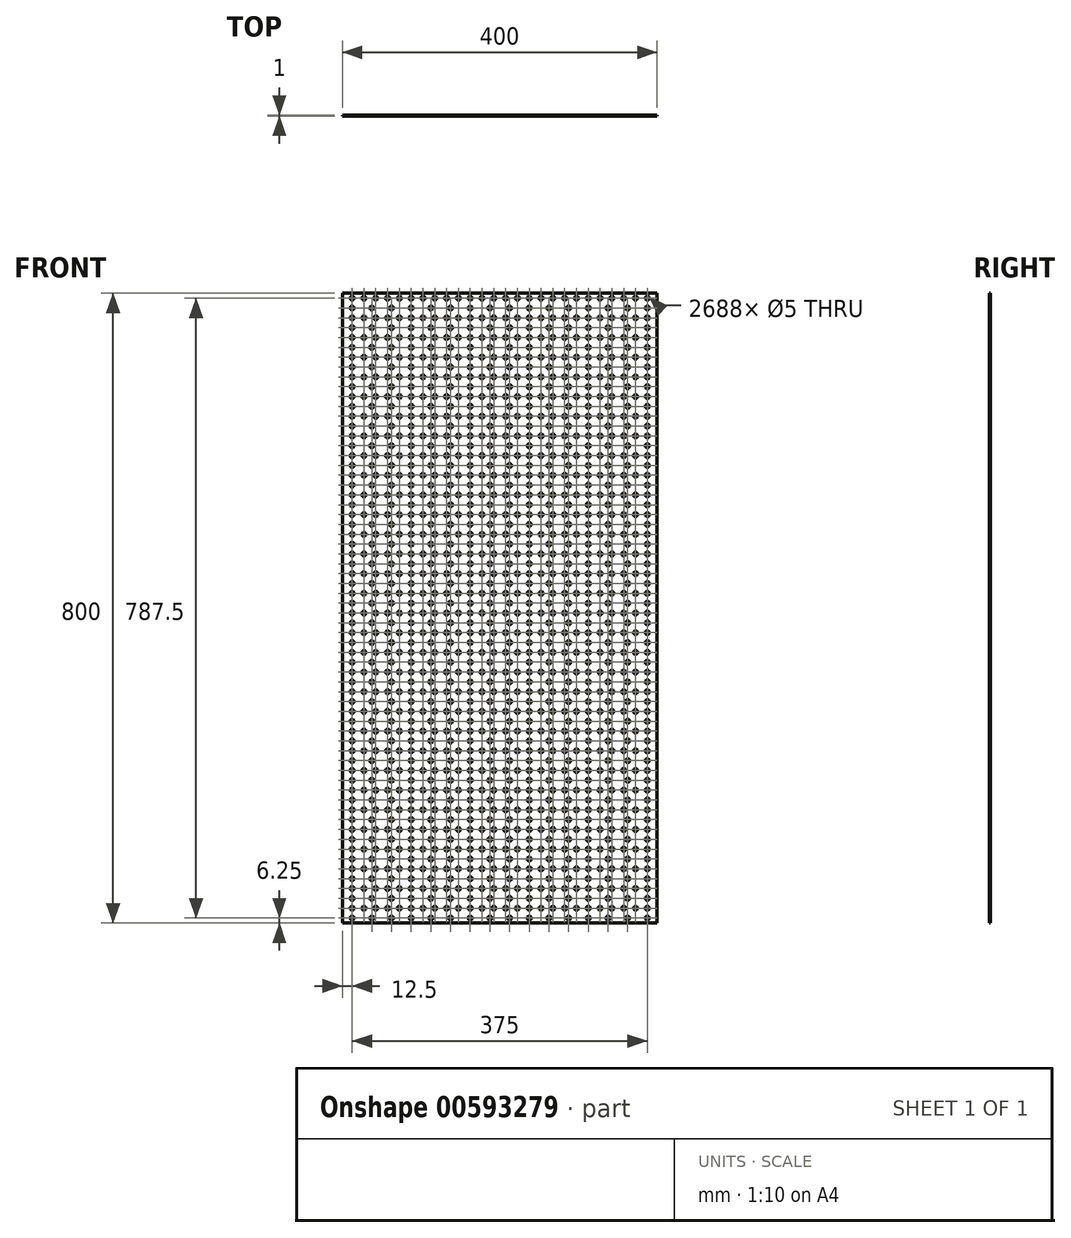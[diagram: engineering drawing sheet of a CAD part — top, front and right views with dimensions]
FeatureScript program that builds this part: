
annotation { "Feature Type Name" : "Feature", "Feature Type Description" : "" }
export const myFeature = defineFeature(function(context is Context, id is Id, definition is map)
    precondition{}
    {
        {
            var Q0;
            Q0=qCreatedBy(makeId("Front.planeOp"),FACE);
            var sketch = newSketch(context, id + "F0", { "sketchPlane" : qUnion([Q0])});
            skLineSegment(sketch, "E0.bottom", {"start": v(200, 400) * mm, "end": v(-200, 400) * mm});
            skLineSegment(sketch, "E0.top", {"start": v(200, -400) * mm, "end": v(-200, -400) * mm});
            skLineSegment(sketch, "E0.left", {"start": v(200, 400) * mm, "end": v(200, -400) * mm});
            skLineSegment(sketch, "E0.right", {"start": v(-200, 400) * mm, "end": v(-200, -400) * mm});
            skPoint(sketch, "E0.middle", {"position": v(0, 0) * mm});
            skCircle(sketch, "E1", {"center": v(-187.5, -393.75) * mm, "radius": 2.5 * mm});
            skCircle(sketch, "E2.1.0.0", {"center": v(-162.5, -393.75) * mm, "radius": 2.5 * mm});
            skCircle(sketch, "E2.2.0.0", {"center": v(-137.5, -393.75) * mm, "radius": 2.5 * mm});
            skCircle(sketch, "E2.3.0.0", {"center": v(-112.5, -393.75) * mm, "radius": 2.5 * mm});
            skCircle(sketch, "E2.4.0.0", {"center": v(-87.5, -393.75) * mm, "radius": 2.5 * mm});
            skCircle(sketch, "E2.5.0.0", {"center": v(-62.5, -393.75) * mm, "radius": 2.5 * mm});
            skCircle(sketch, "E2.6.0.0", {"center": v(-37.5, -393.75) * mm, "radius": 2.5 * mm});
            skCircle(sketch, "E2.7.0.0", {"center": v(-12.5, -393.75) * mm, "radius": 2.5 * mm});
            skCircle(sketch, "E2.8.0.0", {"center": v(12.5, -393.75) * mm, "radius": 2.5 * mm});
            skCircle(sketch, "E2.9.0.0", {"center": v(37.5, -393.75) * mm, "radius": 2.5 * mm});
            skCircle(sketch, "E2.10.0.0", {"center": v(62.5, -393.75) * mm, "radius": 2.5 * mm});
            skCircle(sketch, "E2.11.0.0", {"center": v(87.5, -393.75) * mm, "radius": 2.5 * mm});
            skCircle(sketch, "E2.12.0.0", {"center": v(112.5, -393.75) * mm, "radius": 2.5 * mm});
            skCircle(sketch, "E2.13.0.0", {"center": v(137.5, -393.75) * mm, "radius": 2.5 * mm});
            skCircle(sketch, "E2.14.0.0", {"center": v(162.5, -393.75) * mm, "radius": 2.5 * mm});
            skCircle(sketch, "E2.15.0.0", {"center": v(187.5, -393.75) * mm, "radius": 2.5 * mm});
            skLineSegment(sketch, "E2.direction1", {"start": v(-187.5, -393.75) * mm, "end": v(-162.5, -393.75) * mm, "construction": true});
            skCircle(sketch, "E3.0.1.0", {"center": v(187.5, -368.75) * mm, "radius": 2.5 * mm});
            skCircle(sketch, "E3.0.1.1", {"center": v(37.5, -368.75) * mm, "radius": 2.5 * mm});
            skCircle(sketch, "E3.0.1.2", {"center": v(137.5, -368.75) * mm, "radius": 2.5 * mm});
            skCircle(sketch, "E3.0.1.3", {"center": v(62.5, -368.75) * mm, "radius": 2.5 * mm});
            skCircle(sketch, "E3.0.1.4", {"center": v(87.5, -368.75) * mm, "radius": 2.5 * mm});
            skCircle(sketch, "E3.0.1.5", {"center": v(-137.5, -368.75) * mm, "radius": 2.5 * mm});
            skCircle(sketch, "E3.0.1.6", {"center": v(-112.5, -368.75) * mm, "radius": 2.5 * mm});
            skCircle(sketch, "E3.0.1.7", {"center": v(-87.5, -368.75) * mm, "radius": 2.5 * mm});
            skCircle(sketch, "E3.0.1.8", {"center": v(-62.5, -368.75) * mm, "radius": 2.5 * mm});
            skCircle(sketch, "E3.0.1.9", {"center": v(-37.5, -368.75) * mm, "radius": 2.5 * mm});
            skCircle(sketch, "E3.0.1.10", {"center": v(-12.5, -368.75) * mm, "radius": 2.5 * mm});
            skCircle(sketch, "E3.0.1.11", {"center": v(12.5, -368.75) * mm, "radius": 2.5 * mm});
            skCircle(sketch, "E3.0.1.12", {"center": v(162.5, -368.75) * mm, "radius": 2.5 * mm});
            skCircle(sketch, "E3.0.1.13", {"center": v(112.5, -368.75) * mm, "radius": 2.5 * mm});
            skCircle(sketch, "E3.0.1.14", {"center": v(-187.5, -368.75) * mm, "radius": 2.5 * mm});
            skCircle(sketch, "E3.0.1.15", {"center": v(-162.5, -368.75) * mm, "radius": 2.5 * mm});
            skCircle(sketch, "E3.0.2.0", {"center": v(187.5, -343.75) * mm, "radius": 2.5 * mm});
            skCircle(sketch, "E3.0.2.1", {"center": v(37.5, -343.75) * mm, "radius": 2.5 * mm});
            skCircle(sketch, "E3.0.2.2", {"center": v(137.5, -343.75) * mm, "radius": 2.5 * mm});
            skCircle(sketch, "E3.0.2.3", {"center": v(62.5, -343.75) * mm, "radius": 2.5 * mm});
            skCircle(sketch, "E3.0.2.4", {"center": v(87.5, -343.75) * mm, "radius": 2.5 * mm});
            skCircle(sketch, "E3.0.2.5", {"center": v(-137.5, -343.75) * mm, "radius": 2.5 * mm});
            skCircle(sketch, "E3.0.2.6", {"center": v(-112.5, -343.75) * mm, "radius": 2.5 * mm});
            skCircle(sketch, "E3.0.2.7", {"center": v(-87.5, -343.75) * mm, "radius": 2.5 * mm});
            skCircle(sketch, "E3.0.2.8", {"center": v(-62.5, -343.75) * mm, "radius": 2.5 * mm});
            skCircle(sketch, "E3.0.2.9", {"center": v(-37.5, -343.75) * mm, "radius": 2.5 * mm});
            skCircle(sketch, "E3.0.2.10", {"center": v(-12.5, -343.75) * mm, "radius": 2.5 * mm});
            skCircle(sketch, "E3.0.2.11", {"center": v(12.5, -343.75) * mm, "radius": 2.5 * mm});
            skCircle(sketch, "E3.0.2.12", {"center": v(162.5, -343.75) * mm, "radius": 2.5 * mm});
            skCircle(sketch, "E3.0.2.13", {"center": v(112.5, -343.75) * mm, "radius": 2.5 * mm});
            skCircle(sketch, "E3.0.2.14", {"center": v(-187.5, -343.75) * mm, "radius": 2.5 * mm});
            skCircle(sketch, "E3.0.2.15", {"center": v(-162.5, -343.75) * mm, "radius": 2.5 * mm});
            skCircle(sketch, "E3.0.3.0", {"center": v(187.5, -318.75) * mm, "radius": 2.5 * mm});
            skCircle(sketch, "E3.0.3.1", {"center": v(37.5, -318.75) * mm, "radius": 2.5 * mm});
            skCircle(sketch, "E3.0.3.2", {"center": v(137.5, -318.75) * mm, "radius": 2.5 * mm});
            skCircle(sketch, "E3.0.3.3", {"center": v(62.5, -318.75) * mm, "radius": 2.5 * mm});
            skCircle(sketch, "E3.0.3.4", {"center": v(87.5, -318.75) * mm, "radius": 2.5 * mm});
            skCircle(sketch, "E3.0.3.5", {"center": v(-137.5, -318.75) * mm, "radius": 2.5 * mm});
            skCircle(sketch, "E3.0.3.6", {"center": v(-112.5, -318.75) * mm, "radius": 2.5 * mm});
            skCircle(sketch, "E3.0.3.7", {"center": v(-87.5, -318.75) * mm, "radius": 2.5 * mm});
            skCircle(sketch, "E3.0.3.8", {"center": v(-62.5, -318.75) * mm, "radius": 2.5 * mm});
            skCircle(sketch, "E3.0.3.9", {"center": v(-37.5, -318.75) * mm, "radius": 2.5 * mm});
            skCircle(sketch, "E3.0.3.10", {"center": v(-12.5, -318.75) * mm, "radius": 2.5 * mm});
            skCircle(sketch, "E3.0.3.11", {"center": v(12.5, -318.75) * mm, "radius": 2.5 * mm});
            skCircle(sketch, "E3.0.3.12", {"center": v(162.5, -318.75) * mm, "radius": 2.5 * mm});
            skCircle(sketch, "E3.0.3.13", {"center": v(112.5, -318.75) * mm, "radius": 2.5 * mm});
            skCircle(sketch, "E3.0.3.14", {"center": v(-187.5, -318.75) * mm, "radius": 2.5 * mm});
            skCircle(sketch, "E3.0.3.15", {"center": v(-162.5, -318.75) * mm, "radius": 2.5 * mm});
            skCircle(sketch, "E3.0.4.0", {"center": v(187.5, -293.75) * mm, "radius": 2.5 * mm});
            skCircle(sketch, "E3.0.4.1", {"center": v(37.5, -293.75) * mm, "radius": 2.5 * mm});
            skCircle(sketch, "E3.0.4.2", {"center": v(137.5, -293.75) * mm, "radius": 2.5 * mm});
            skCircle(sketch, "E3.0.4.3", {"center": v(62.5, -293.75) * mm, "radius": 2.5 * mm});
            skCircle(sketch, "E3.0.4.4", {"center": v(87.5, -293.75) * mm, "radius": 2.5 * mm});
            skCircle(sketch, "E3.0.4.5", {"center": v(-137.5, -293.75) * mm, "radius": 2.5 * mm});
            skCircle(sketch, "E3.0.4.6", {"center": v(-112.5, -293.75) * mm, "radius": 2.5 * mm});
            skCircle(sketch, "E3.0.4.7", {"center": v(-87.5, -293.75) * mm, "radius": 2.5 * mm});
            skCircle(sketch, "E3.0.4.8", {"center": v(-62.5, -293.75) * mm, "radius": 2.5 * mm});
            skCircle(sketch, "E3.0.4.9", {"center": v(-37.5, -293.75) * mm, "radius": 2.5 * mm});
            skCircle(sketch, "E3.0.4.10", {"center": v(-12.5, -293.75) * mm, "radius": 2.5 * mm});
            skCircle(sketch, "E3.0.4.11", {"center": v(12.5, -293.75) * mm, "radius": 2.5 * mm});
            skCircle(sketch, "E3.0.4.12", {"center": v(162.5, -293.75) * mm, "radius": 2.5 * mm});
            skCircle(sketch, "E3.0.4.13", {"center": v(112.5, -293.75) * mm, "radius": 2.5 * mm});
            skCircle(sketch, "E3.0.4.14", {"center": v(-187.5, -293.75) * mm, "radius": 2.5 * mm});
            skCircle(sketch, "E3.0.4.15", {"center": v(-162.5, -293.75) * mm, "radius": 2.5 * mm});
            skCircle(sketch, "E3.0.5.0", {"center": v(187.5, -268.75) * mm, "radius": 2.5 * mm});
            skCircle(sketch, "E3.0.5.1", {"center": v(37.5, -268.75) * mm, "radius": 2.5 * mm});
            skCircle(sketch, "E3.0.5.2", {"center": v(137.5, -268.75) * mm, "radius": 2.5 * mm});
            skCircle(sketch, "E3.0.5.3", {"center": v(62.5, -268.75) * mm, "radius": 2.5 * mm});
            skCircle(sketch, "E3.0.5.4", {"center": v(87.5, -268.75) * mm, "radius": 2.5 * mm});
            skCircle(sketch, "E3.0.5.5", {"center": v(-137.5, -268.75) * mm, "radius": 2.5 * mm});
            skCircle(sketch, "E3.0.5.6", {"center": v(-112.5, -268.75) * mm, "radius": 2.5 * mm});
            skCircle(sketch, "E3.0.5.7", {"center": v(-87.5, -268.75) * mm, "radius": 2.5 * mm});
            skCircle(sketch, "E3.0.5.8", {"center": v(-62.5, -268.75) * mm, "radius": 2.5 * mm});
            skCircle(sketch, "E3.0.5.9", {"center": v(-37.5, -268.75) * mm, "radius": 2.5 * mm});
            skCircle(sketch, "E3.0.5.10", {"center": v(-12.5, -268.75) * mm, "radius": 2.5 * mm});
            skCircle(sketch, "E3.0.5.11", {"center": v(12.5, -268.75) * mm, "radius": 2.5 * mm});
            skCircle(sketch, "E3.0.5.12", {"center": v(162.5, -268.75) * mm, "radius": 2.5 * mm});
            skCircle(sketch, "E3.0.5.13", {"center": v(112.5, -268.75) * mm, "radius": 2.5 * mm});
            skCircle(sketch, "E3.0.5.14", {"center": v(-187.5, -268.75) * mm, "radius": 2.5 * mm});
            skCircle(sketch, "E3.0.5.15", {"center": v(-162.5, -268.75) * mm, "radius": 2.5 * mm});
            skCircle(sketch, "E3.0.6.0", {"center": v(187.5, -243.75) * mm, "radius": 2.5 * mm});
            skCircle(sketch, "E3.0.6.1", {"center": v(37.5, -243.75) * mm, "radius": 2.5 * mm});
            skCircle(sketch, "E3.0.6.2", {"center": v(137.5, -243.75) * mm, "radius": 2.5 * mm});
            skCircle(sketch, "E3.0.6.3", {"center": v(62.5, -243.75) * mm, "radius": 2.5 * mm});
            skCircle(sketch, "E3.0.6.4", {"center": v(87.5, -243.75) * mm, "radius": 2.5 * mm});
            skCircle(sketch, "E3.0.6.5", {"center": v(-137.5, -243.75) * mm, "radius": 2.5 * mm});
            skCircle(sketch, "E3.0.6.6", {"center": v(-112.5, -243.75) * mm, "radius": 2.5 * mm});
            skCircle(sketch, "E3.0.6.7", {"center": v(-87.5, -243.75) * mm, "radius": 2.5 * mm});
            skCircle(sketch, "E3.0.6.8", {"center": v(-62.5, -243.75) * mm, "radius": 2.5 * mm});
            skCircle(sketch, "E3.0.6.9", {"center": v(-37.5, -243.75) * mm, "radius": 2.5 * mm});
            skCircle(sketch, "E3.0.6.10", {"center": v(-12.5, -243.75) * mm, "radius": 2.5 * mm});
            skCircle(sketch, "E3.0.6.11", {"center": v(12.5, -243.75) * mm, "radius": 2.5 * mm});
            skCircle(sketch, "E3.0.6.12", {"center": v(162.5, -243.75) * mm, "radius": 2.5 * mm});
            skCircle(sketch, "E3.0.6.13", {"center": v(112.5, -243.75) * mm, "radius": 2.5 * mm});
            skCircle(sketch, "E3.0.6.14", {"center": v(-187.5, -243.75) * mm, "radius": 2.5 * mm});
            skCircle(sketch, "E3.0.6.15", {"center": v(-162.5, -243.75) * mm, "radius": 2.5 * mm});
            skCircle(sketch, "E3.0.7.0", {"center": v(187.5, -218.75) * mm, "radius": 2.5 * mm});
            skCircle(sketch, "E3.0.7.1", {"center": v(37.5, -218.75) * mm, "radius": 2.5 * mm});
            skCircle(sketch, "E3.0.7.2", {"center": v(137.5, -218.75) * mm, "radius": 2.5 * mm});
            skCircle(sketch, "E3.0.7.3", {"center": v(62.5, -218.75) * mm, "radius": 2.5 * mm});
            skCircle(sketch, "E3.0.7.4", {"center": v(87.5, -218.75) * mm, "radius": 2.5 * mm});
            skCircle(sketch, "E3.0.7.5", {"center": v(-137.5, -218.75) * mm, "radius": 2.5 * mm});
            skCircle(sketch, "E3.0.7.6", {"center": v(-112.5, -218.75) * mm, "radius": 2.5 * mm});
            skCircle(sketch, "E3.0.7.7", {"center": v(-87.5, -218.75) * mm, "radius": 2.5 * mm});
            skCircle(sketch, "E3.0.7.8", {"center": v(-62.5, -218.75) * mm, "radius": 2.5 * mm});
            skCircle(sketch, "E3.0.7.9", {"center": v(-37.5, -218.75) * mm, "radius": 2.5 * mm});
            skCircle(sketch, "E3.0.7.10", {"center": v(-12.5, -218.75) * mm, "radius": 2.5 * mm});
            skCircle(sketch, "E3.0.7.11", {"center": v(12.5, -218.75) * mm, "radius": 2.5 * mm});
            skCircle(sketch, "E3.0.7.12", {"center": v(162.5, -218.75) * mm, "radius": 2.5 * mm});
            skCircle(sketch, "E3.0.7.13", {"center": v(112.5, -218.75) * mm, "radius": 2.5 * mm});
            skCircle(sketch, "E3.0.7.14", {"center": v(-187.5, -218.75) * mm, "radius": 2.5 * mm});
            skCircle(sketch, "E3.0.7.15", {"center": v(-162.5, -218.75) * mm, "radius": 2.5 * mm});
            skCircle(sketch, "E3.0.8.0", {"center": v(187.5, -193.75) * mm, "radius": 2.5 * mm});
            skCircle(sketch, "E3.0.8.1", {"center": v(37.5, -193.75) * mm, "radius": 2.5 * mm});
            skCircle(sketch, "E3.0.8.2", {"center": v(137.5, -193.75) * mm, "radius": 2.5 * mm});
            skCircle(sketch, "E3.0.8.3", {"center": v(62.5, -193.75) * mm, "radius": 2.5 * mm});
            skCircle(sketch, "E3.0.8.4", {"center": v(87.5, -193.75) * mm, "radius": 2.5 * mm});
            skCircle(sketch, "E3.0.8.5", {"center": v(-137.5, -193.75) * mm, "radius": 2.5 * mm});
            skCircle(sketch, "E3.0.8.6", {"center": v(-112.5, -193.75) * mm, "radius": 2.5 * mm});
            skCircle(sketch, "E3.0.8.7", {"center": v(-87.5, -193.75) * mm, "radius": 2.5 * mm});
            skCircle(sketch, "E3.0.8.8", {"center": v(-62.5, -193.75) * mm, "radius": 2.5 * mm});
            skCircle(sketch, "E3.0.8.9", {"center": v(-37.5, -193.75) * mm, "radius": 2.5 * mm});
            skCircle(sketch, "E3.0.8.10", {"center": v(-12.5, -193.75) * mm, "radius": 2.5 * mm});
            skCircle(sketch, "E3.0.8.11", {"center": v(12.5, -193.75) * mm, "radius": 2.5 * mm});
            skCircle(sketch, "E3.0.8.12", {"center": v(162.5, -193.75) * mm, "radius": 2.5 * mm});
            skCircle(sketch, "E3.0.8.13", {"center": v(112.5, -193.75) * mm, "radius": 2.5 * mm});
            skCircle(sketch, "E3.0.8.14", {"center": v(-187.5, -193.75) * mm, "radius": 2.5 * mm});
            skCircle(sketch, "E3.0.8.15", {"center": v(-162.5, -193.75) * mm, "radius": 2.5 * mm});
            skCircle(sketch, "E3.0.9.0", {"center": v(187.5, -168.75) * mm, "radius": 2.5 * mm});
            skCircle(sketch, "E3.0.9.1", {"center": v(37.5, -168.75) * mm, "radius": 2.5 * mm});
            skCircle(sketch, "E3.0.9.2", {"center": v(137.5, -168.75) * mm, "radius": 2.5 * mm});
            skCircle(sketch, "E3.0.9.3", {"center": v(62.5, -168.75) * mm, "radius": 2.5 * mm});
            skCircle(sketch, "E3.0.9.4", {"center": v(87.5, -168.75) * mm, "radius": 2.5 * mm});
            skCircle(sketch, "E3.0.9.5", {"center": v(-137.5, -168.75) * mm, "radius": 2.5 * mm});
            skCircle(sketch, "E3.0.9.6", {"center": v(-112.5, -168.75) * mm, "radius": 2.5 * mm});
            skCircle(sketch, "E3.0.9.7", {"center": v(-87.5, -168.75) * mm, "radius": 2.5 * mm});
            skCircle(sketch, "E3.0.9.8", {"center": v(-62.5, -168.75) * mm, "radius": 2.5 * mm});
            skCircle(sketch, "E3.0.9.9", {"center": v(-37.5, -168.75) * mm, "radius": 2.5 * mm});
            skCircle(sketch, "E3.0.9.10", {"center": v(-12.5, -168.75) * mm, "radius": 2.5 * mm});
            skCircle(sketch, "E3.0.9.11", {"center": v(12.5, -168.75) * mm, "radius": 2.5 * mm});
            skCircle(sketch, "E3.0.9.12", {"center": v(162.5, -168.75) * mm, "radius": 2.5 * mm});
            skCircle(sketch, "E3.0.9.13", {"center": v(112.5, -168.75) * mm, "radius": 2.5 * mm});
            skCircle(sketch, "E3.0.9.14", {"center": v(-187.5, -168.75) * mm, "radius": 2.5 * mm});
            skCircle(sketch, "E3.0.9.15", {"center": v(-162.5, -168.75) * mm, "radius": 2.5 * mm});
            skCircle(sketch, "E3.0.10.0", {"center": v(187.5, -143.75) * mm, "radius": 2.5 * mm});
            skCircle(sketch, "E3.0.10.1", {"center": v(37.5, -143.75) * mm, "radius": 2.5 * mm});
            skCircle(sketch, "E3.0.10.2", {"center": v(137.5, -143.75) * mm, "radius": 2.5 * mm});
            skCircle(sketch, "E3.0.10.3", {"center": v(62.5, -143.75) * mm, "radius": 2.5 * mm});
            skCircle(sketch, "E3.0.10.4", {"center": v(87.5, -143.75) * mm, "radius": 2.5 * mm});
            skCircle(sketch, "E3.0.10.5", {"center": v(-137.5, -143.75) * mm, "radius": 2.5 * mm});
            skCircle(sketch, "E3.0.10.6", {"center": v(-112.5, -143.75) * mm, "radius": 2.5 * mm});
            skCircle(sketch, "E3.0.10.7", {"center": v(-87.5, -143.75) * mm, "radius": 2.5 * mm});
            skCircle(sketch, "E3.0.10.8", {"center": v(-62.5, -143.75) * mm, "radius": 2.5 * mm});
            skCircle(sketch, "E3.0.10.9", {"center": v(-37.5, -143.75) * mm, "radius": 2.5 * mm});
            skCircle(sketch, "E3.0.10.10", {"center": v(-12.5, -143.75) * mm, "radius": 2.5 * mm});
            skCircle(sketch, "E3.0.10.11", {"center": v(12.5, -143.75) * mm, "radius": 2.5 * mm});
            skCircle(sketch, "E3.0.10.12", {"center": v(162.5, -143.75) * mm, "radius": 2.5 * mm});
            skCircle(sketch, "E3.0.10.13", {"center": v(112.5, -143.75) * mm, "radius": 2.5 * mm});
            skCircle(sketch, "E3.0.10.14", {"center": v(-187.5, -143.75) * mm, "radius": 2.5 * mm});
            skCircle(sketch, "E3.0.10.15", {"center": v(-162.5, -143.75) * mm, "radius": 2.5 * mm});
            skCircle(sketch, "E3.0.11.0", {"center": v(187.5, -118.75) * mm, "radius": 2.5 * mm});
            skCircle(sketch, "E3.0.11.1", {"center": v(37.5, -118.75) * mm, "radius": 2.5 * mm});
            skCircle(sketch, "E3.0.11.2", {"center": v(137.5, -118.75) * mm, "radius": 2.5 * mm});
            skCircle(sketch, "E3.0.11.3", {"center": v(62.5, -118.75) * mm, "radius": 2.5 * mm});
            skCircle(sketch, "E3.0.11.4", {"center": v(87.5, -118.75) * mm, "radius": 2.5 * mm});
            skCircle(sketch, "E3.0.11.5", {"center": v(-137.5, -118.75) * mm, "radius": 2.5 * mm});
            skCircle(sketch, "E3.0.11.6", {"center": v(-112.5, -118.75) * mm, "radius": 2.5 * mm});
            skCircle(sketch, "E3.0.11.7", {"center": v(-87.5, -118.75) * mm, "radius": 2.5 * mm});
            skCircle(sketch, "E3.0.11.8", {"center": v(-62.5, -118.75) * mm, "radius": 2.5 * mm});
            skCircle(sketch, "E3.0.11.9", {"center": v(-37.5, -118.75) * mm, "radius": 2.5 * mm});
            skCircle(sketch, "E3.0.11.10", {"center": v(-12.5, -118.75) * mm, "radius": 2.5 * mm});
            skCircle(sketch, "E3.0.11.11", {"center": v(12.5, -118.75) * mm, "radius": 2.5 * mm});
            skCircle(sketch, "E3.0.11.12", {"center": v(162.5, -118.75) * mm, "radius": 2.5 * mm});
            skCircle(sketch, "E3.0.11.13", {"center": v(112.5, -118.75) * mm, "radius": 2.5 * mm});
            skCircle(sketch, "E3.0.11.14", {"center": v(-187.5, -118.75) * mm, "radius": 2.5 * mm});
            skCircle(sketch, "E3.0.11.15", {"center": v(-162.5, -118.75) * mm, "radius": 2.5 * mm});
            skCircle(sketch, "E3.0.12.0", {"center": v(187.5, -93.75) * mm, "radius": 2.5 * mm});
            skCircle(sketch, "E3.0.12.1", {"center": v(37.5, -93.75) * mm, "radius": 2.5 * mm});
            skCircle(sketch, "E3.0.12.2", {"center": v(137.5, -93.75) * mm, "radius": 2.5 * mm});
            skCircle(sketch, "E3.0.12.3", {"center": v(62.5, -93.75) * mm, "radius": 2.5 * mm});
            skCircle(sketch, "E3.0.12.4", {"center": v(87.5, -93.75) * mm, "radius": 2.5 * mm});
            skCircle(sketch, "E3.0.12.5", {"center": v(-137.5, -93.75) * mm, "radius": 2.5 * mm});
            skCircle(sketch, "E3.0.12.6", {"center": v(-112.5, -93.75) * mm, "radius": 2.5 * mm});
            skCircle(sketch, "E3.0.12.7", {"center": v(-87.5, -93.75) * mm, "radius": 2.5 * mm});
            skCircle(sketch, "E3.0.12.8", {"center": v(-62.5, -93.75) * mm, "radius": 2.5 * mm});
            skCircle(sketch, "E3.0.12.9", {"center": v(-37.5, -93.75) * mm, "radius": 2.5 * mm});
            skCircle(sketch, "E3.0.12.10", {"center": v(-12.5, -93.75) * mm, "radius": 2.5 * mm});
            skCircle(sketch, "E3.0.12.11", {"center": v(12.5, -93.75) * mm, "radius": 2.5 * mm});
            skCircle(sketch, "E3.0.12.12", {"center": v(162.5, -93.75) * mm, "radius": 2.5 * mm});
            skCircle(sketch, "E3.0.12.13", {"center": v(112.5, -93.75) * mm, "radius": 2.5 * mm});
            skCircle(sketch, "E3.0.12.14", {"center": v(-187.5, -93.75) * mm, "radius": 2.5 * mm});
            skCircle(sketch, "E3.0.12.15", {"center": v(-162.5, -93.75) * mm, "radius": 2.5 * mm});
            skCircle(sketch, "E3.0.13.0", {"center": v(187.5, -68.75) * mm, "radius": 2.5 * mm});
            skCircle(sketch, "E3.0.13.1", {"center": v(37.5, -68.75) * mm, "radius": 2.5 * mm});
            skCircle(sketch, "E3.0.13.2", {"center": v(137.5, -68.75) * mm, "radius": 2.5 * mm});
            skCircle(sketch, "E3.0.13.3", {"center": v(62.5, -68.75) * mm, "radius": 2.5 * mm});
            skCircle(sketch, "E3.0.13.4", {"center": v(87.5, -68.75) * mm, "radius": 2.5 * mm});
            skCircle(sketch, "E3.0.13.5", {"center": v(-137.5, -68.75) * mm, "radius": 2.5 * mm});
            skCircle(sketch, "E3.0.13.6", {"center": v(-112.5, -68.75) * mm, "radius": 2.5 * mm});
            skCircle(sketch, "E3.0.13.7", {"center": v(-87.5, -68.75) * mm, "radius": 2.5 * mm});
            skCircle(sketch, "E3.0.13.8", {"center": v(-62.5, -68.75) * mm, "radius": 2.5 * mm});
            skCircle(sketch, "E3.0.13.9", {"center": v(-37.5, -68.75) * mm, "radius": 2.5 * mm});
            skCircle(sketch, "E3.0.13.10", {"center": v(-12.5, -68.75) * mm, "radius": 2.5 * mm});
            skCircle(sketch, "E3.0.13.11", {"center": v(12.5, -68.75) * mm, "radius": 2.5 * mm});
            skCircle(sketch, "E3.0.13.12", {"center": v(162.5, -68.75) * mm, "radius": 2.5 * mm});
            skCircle(sketch, "E3.0.13.13", {"center": v(112.5, -68.75) * mm, "radius": 2.5 * mm});
            skCircle(sketch, "E3.0.13.14", {"center": v(-187.5, -68.75) * mm, "radius": 2.5 * mm});
            skCircle(sketch, "E3.0.13.15", {"center": v(-162.5, -68.75) * mm, "radius": 2.5 * mm});
            skCircle(sketch, "E3.0.14.0", {"center": v(187.5, -43.75) * mm, "radius": 2.5 * mm});
            skCircle(sketch, "E3.0.14.1", {"center": v(37.5, -43.75) * mm, "radius": 2.5 * mm});
            skCircle(sketch, "E3.0.14.2", {"center": v(137.5, -43.75) * mm, "radius": 2.5 * mm});
            skCircle(sketch, "E3.0.14.3", {"center": v(62.5, -43.75) * mm, "radius": 2.5 * mm});
            skCircle(sketch, "E3.0.14.4", {"center": v(87.5, -43.75) * mm, "radius": 2.5 * mm});
            skCircle(sketch, "E3.0.14.5", {"center": v(-137.5, -43.75) * mm, "radius": 2.5 * mm});
            skCircle(sketch, "E3.0.14.6", {"center": v(-112.5, -43.75) * mm, "radius": 2.5 * mm});
            skCircle(sketch, "E3.0.14.7", {"center": v(-87.5, -43.75) * mm, "radius": 2.5 * mm});
            skCircle(sketch, "E3.0.14.8", {"center": v(-62.5, -43.75) * mm, "radius": 2.5 * mm});
            skCircle(sketch, "E3.0.14.9", {"center": v(-37.5, -43.75) * mm, "radius": 2.5 * mm});
            skCircle(sketch, "E3.0.14.10", {"center": v(-12.5, -43.75) * mm, "radius": 2.5 * mm});
            skCircle(sketch, "E3.0.14.11", {"center": v(12.5, -43.75) * mm, "radius": 2.5 * mm});
            skCircle(sketch, "E3.0.14.12", {"center": v(162.5, -43.75) * mm, "radius": 2.5 * mm});
            skCircle(sketch, "E3.0.14.13", {"center": v(112.5, -43.75) * mm, "radius": 2.5 * mm});
            skCircle(sketch, "E3.0.14.14", {"center": v(-187.5, -43.75) * mm, "radius": 2.5 * mm});
            skCircle(sketch, "E3.0.14.15", {"center": v(-162.5, -43.75) * mm, "radius": 2.5 * mm});
            skCircle(sketch, "E3.0.15.0", {"center": v(187.5, -18.75) * mm, "radius": 2.5 * mm});
            skCircle(sketch, "E3.0.15.1", {"center": v(37.5, -18.75) * mm, "radius": 2.5 * mm});
            skCircle(sketch, "E3.0.15.2", {"center": v(137.5, -18.75) * mm, "radius": 2.5 * mm});
            skCircle(sketch, "E3.0.15.3", {"center": v(62.5, -18.75) * mm, "radius": 2.5 * mm});
            skCircle(sketch, "E3.0.15.4", {"center": v(87.5, -18.75) * mm, "radius": 2.5 * mm});
            skCircle(sketch, "E3.0.15.5", {"center": v(-137.5, -18.75) * mm, "radius": 2.5 * mm});
            skCircle(sketch, "E3.0.15.6", {"center": v(-112.5, -18.75) * mm, "radius": 2.5 * mm});
            skCircle(sketch, "E3.0.15.7", {"center": v(-87.5, -18.75) * mm, "radius": 2.5 * mm});
            skCircle(sketch, "E3.0.15.8", {"center": v(-62.5, -18.75) * mm, "radius": 2.5 * mm});
            skCircle(sketch, "E3.0.15.9", {"center": v(-37.5, -18.75) * mm, "radius": 2.5 * mm});
            skCircle(sketch, "E3.0.15.10", {"center": v(-12.5, -18.75) * mm, "radius": 2.5 * mm});
            skCircle(sketch, "E3.0.15.11", {"center": v(12.5, -18.75) * mm, "radius": 2.5 * mm});
            skCircle(sketch, "E3.0.15.12", {"center": v(162.5, -18.75) * mm, "radius": 2.5 * mm});
            skCircle(sketch, "E3.0.15.13", {"center": v(112.5, -18.75) * mm, "radius": 2.5 * mm});
            skCircle(sketch, "E3.0.15.14", {"center": v(-187.5, -18.75) * mm, "radius": 2.5 * mm});
            skCircle(sketch, "E3.0.15.15", {"center": v(-162.5, -18.75) * mm, "radius": 2.5 * mm});
            skCircle(sketch, "E3.0.16.0", {"center": v(187.5, 6.25) * mm, "radius": 2.5 * mm});
            skCircle(sketch, "E3.0.16.1", {"center": v(37.5, 6.25) * mm, "radius": 2.5 * mm});
            skCircle(sketch, "E3.0.16.2", {"center": v(137.5, 6.25) * mm, "radius": 2.5 * mm});
            skCircle(sketch, "E3.0.16.3", {"center": v(62.5, 6.25) * mm, "radius": 2.5 * mm});
            skCircle(sketch, "E3.0.16.4", {"center": v(87.5, 6.25) * mm, "radius": 2.5 * mm});
            skCircle(sketch, "E3.0.16.5", {"center": v(-137.5, 6.25) * mm, "radius": 2.5 * mm});
            skCircle(sketch, "E3.0.16.6", {"center": v(-112.5, 6.25) * mm, "radius": 2.5 * mm});
            skCircle(sketch, "E3.0.16.7", {"center": v(-87.5, 6.25) * mm, "radius": 2.5 * mm});
            skCircle(sketch, "E3.0.16.8", {"center": v(-62.5, 6.25) * mm, "radius": 2.5 * mm});
            skCircle(sketch, "E3.0.16.9", {"center": v(-37.5, 6.25) * mm, "radius": 2.5 * mm});
            skCircle(sketch, "E3.0.16.10", {"center": v(-12.5, 6.25) * mm, "radius": 2.5 * mm});
            skCircle(sketch, "E3.0.16.11", {"center": v(12.5, 6.25) * mm, "radius": 2.5 * mm});
            skCircle(sketch, "E3.0.16.12", {"center": v(162.5, 6.25) * mm, "radius": 2.5 * mm});
            skCircle(sketch, "E3.0.16.13", {"center": v(112.5, 6.25) * mm, "radius": 2.5 * mm});
            skCircle(sketch, "E3.0.16.14", {"center": v(-187.5, 6.25) * mm, "radius": 2.5 * mm});
            skCircle(sketch, "E3.0.16.15", {"center": v(-162.5, 6.25) * mm, "radius": 2.5 * mm});
            skCircle(sketch, "E3.0.17.0", {"center": v(187.5, 31.25) * mm, "radius": 2.5 * mm});
            skCircle(sketch, "E3.0.17.1", {"center": v(37.5, 31.25) * mm, "radius": 2.5 * mm});
            skCircle(sketch, "E3.0.17.2", {"center": v(137.5, 31.25) * mm, "radius": 2.5 * mm});
            skCircle(sketch, "E3.0.17.3", {"center": v(62.5, 31.25) * mm, "radius": 2.5 * mm});
            skCircle(sketch, "E3.0.17.4", {"center": v(87.5, 31.25) * mm, "radius": 2.5 * mm});
            skCircle(sketch, "E3.0.17.5", {"center": v(-137.5, 31.25) * mm, "radius": 2.5 * mm});
            skCircle(sketch, "E3.0.17.6", {"center": v(-112.5, 31.25) * mm, "radius": 2.5 * mm});
            skCircle(sketch, "E3.0.17.7", {"center": v(-87.5, 31.25) * mm, "radius": 2.5 * mm});
            skCircle(sketch, "E3.0.17.8", {"center": v(-62.5, 31.25) * mm, "radius": 2.5 * mm});
            skCircle(sketch, "E3.0.17.9", {"center": v(-37.5, 31.25) * mm, "radius": 2.5 * mm});
            skCircle(sketch, "E3.0.17.10", {"center": v(-12.5, 31.25) * mm, "radius": 2.5 * mm});
            skCircle(sketch, "E3.0.17.11", {"center": v(12.5, 31.25) * mm, "radius": 2.5 * mm});
            skCircle(sketch, "E3.0.17.12", {"center": v(162.5, 31.25) * mm, "radius": 2.5 * mm});
            skCircle(sketch, "E3.0.17.13", {"center": v(112.5, 31.25) * mm, "radius": 2.5 * mm});
            skCircle(sketch, "E3.0.17.14", {"center": v(-187.5, 31.25) * mm, "radius": 2.5 * mm});
            skCircle(sketch, "E3.0.17.15", {"center": v(-162.5, 31.25) * mm, "radius": 2.5 * mm});
            skCircle(sketch, "E3.0.18.0", {"center": v(187.5, 56.25) * mm, "radius": 2.5 * mm});
            skCircle(sketch, "E3.0.18.1", {"center": v(37.5, 56.25) * mm, "radius": 2.5 * mm});
            skCircle(sketch, "E3.0.18.2", {"center": v(137.5, 56.25) * mm, "radius": 2.5 * mm});
            skCircle(sketch, "E3.0.18.3", {"center": v(62.5, 56.25) * mm, "radius": 2.5 * mm});
            skCircle(sketch, "E3.0.18.4", {"center": v(87.5, 56.25) * mm, "radius": 2.5 * mm});
            skCircle(sketch, "E3.0.18.5", {"center": v(-137.5, 56.25) * mm, "radius": 2.5 * mm});
            skCircle(sketch, "E3.0.18.6", {"center": v(-112.5, 56.25) * mm, "radius": 2.5 * mm});
            skCircle(sketch, "E3.0.18.7", {"center": v(-87.5, 56.25) * mm, "radius": 2.5 * mm});
            skCircle(sketch, "E3.0.18.8", {"center": v(-62.5, 56.25) * mm, "radius": 2.5 * mm});
            skCircle(sketch, "E3.0.18.9", {"center": v(-37.5, 56.25) * mm, "radius": 2.5 * mm});
            skCircle(sketch, "E3.0.18.10", {"center": v(-12.5, 56.25) * mm, "radius": 2.5 * mm});
            skCircle(sketch, "E3.0.18.11", {"center": v(12.5, 56.25) * mm, "radius": 2.5 * mm});
            skCircle(sketch, "E3.0.18.12", {"center": v(162.5, 56.25) * mm, "radius": 2.5 * mm});
            skCircle(sketch, "E3.0.18.13", {"center": v(112.5, 56.25) * mm, "radius": 2.5 * mm});
            skCircle(sketch, "E3.0.18.14", {"center": v(-187.5, 56.25) * mm, "radius": 2.5 * mm});
            skCircle(sketch, "E3.0.18.15", {"center": v(-162.5, 56.25) * mm, "radius": 2.5 * mm});
            skCircle(sketch, "E3.0.19.0", {"center": v(187.5, 81.25) * mm, "radius": 2.5 * mm});
            skCircle(sketch, "E3.0.19.1", {"center": v(37.5, 81.25) * mm, "radius": 2.5 * mm});
            skCircle(sketch, "E3.0.19.2", {"center": v(137.5, 81.25) * mm, "radius": 2.5 * mm});
            skCircle(sketch, "E3.0.19.3", {"center": v(62.5, 81.25) * mm, "radius": 2.5 * mm});
            skCircle(sketch, "E3.0.19.4", {"center": v(87.5, 81.25) * mm, "radius": 2.5 * mm});
            skCircle(sketch, "E3.0.19.5", {"center": v(-137.5, 81.25) * mm, "radius": 2.5 * mm});
            skCircle(sketch, "E3.0.19.6", {"center": v(-112.5, 81.25) * mm, "radius": 2.5 * mm});
            skCircle(sketch, "E3.0.19.7", {"center": v(-87.5, 81.25) * mm, "radius": 2.5 * mm});
            skCircle(sketch, "E3.0.19.8", {"center": v(-62.5, 81.25) * mm, "radius": 2.5 * mm});
            skCircle(sketch, "E3.0.19.9", {"center": v(-37.5, 81.25) * mm, "radius": 2.5 * mm});
            skCircle(sketch, "E3.0.19.10", {"center": v(-12.5, 81.25) * mm, "radius": 2.5 * mm});
            skCircle(sketch, "E3.0.19.11", {"center": v(12.5, 81.25) * mm, "radius": 2.5 * mm});
            skCircle(sketch, "E3.0.19.12", {"center": v(162.5, 81.25) * mm, "radius": 2.5 * mm});
            skCircle(sketch, "E3.0.19.13", {"center": v(112.5, 81.25) * mm, "radius": 2.5 * mm});
            skCircle(sketch, "E3.0.19.14", {"center": v(-187.5, 81.25) * mm, "radius": 2.5 * mm});
            skCircle(sketch, "E3.0.19.15", {"center": v(-162.5, 81.25) * mm, "radius": 2.5 * mm});
            skCircle(sketch, "E3.0.20.0", {"center": v(187.5, 106.25) * mm, "radius": 2.5 * mm});
            skCircle(sketch, "E3.0.20.1", {"center": v(37.5, 106.25) * mm, "radius": 2.5 * mm});
            skCircle(sketch, "E3.0.20.2", {"center": v(137.5, 106.25) * mm, "radius": 2.5 * mm});
            skCircle(sketch, "E3.0.20.3", {"center": v(62.5, 106.25) * mm, "radius": 2.5 * mm});
            skCircle(sketch, "E3.0.20.4", {"center": v(87.5, 106.25) * mm, "radius": 2.5 * mm});
            skCircle(sketch, "E3.0.20.5", {"center": v(-137.5, 106.25) * mm, "radius": 2.5 * mm});
            skCircle(sketch, "E3.0.20.6", {"center": v(-112.5, 106.25) * mm, "radius": 2.5 * mm});
            skCircle(sketch, "E3.0.20.7", {"center": v(-87.5, 106.25) * mm, "radius": 2.5 * mm});
            skCircle(sketch, "E3.0.20.8", {"center": v(-62.5, 106.25) * mm, "radius": 2.5 * mm});
            skCircle(sketch, "E3.0.20.9", {"center": v(-37.5, 106.25) * mm, "radius": 2.5 * mm});
            skCircle(sketch, "E3.0.20.10", {"center": v(-12.5, 106.25) * mm, "radius": 2.5 * mm});
            skCircle(sketch, "E3.0.20.11", {"center": v(12.5, 106.25) * mm, "radius": 2.5 * mm});
            skCircle(sketch, "E3.0.20.12", {"center": v(162.5, 106.25) * mm, "radius": 2.5 * mm});
            skCircle(sketch, "E3.0.20.13", {"center": v(112.5, 106.25) * mm, "radius": 2.5 * mm});
            skCircle(sketch, "E3.0.20.14", {"center": v(-187.5, 106.25) * mm, "radius": 2.5 * mm});
            skCircle(sketch, "E3.0.20.15", {"center": v(-162.5, 106.25) * mm, "radius": 2.5 * mm});
            skCircle(sketch, "E3.0.21.0", {"center": v(187.5, 131.25) * mm, "radius": 2.5 * mm});
            skCircle(sketch, "E3.0.21.1", {"center": v(37.5, 131.25) * mm, "radius": 2.5 * mm});
            skCircle(sketch, "E3.0.21.2", {"center": v(137.5, 131.25) * mm, "radius": 2.5 * mm});
            skCircle(sketch, "E3.0.21.3", {"center": v(62.5, 131.25) * mm, "radius": 2.5 * mm});
            skCircle(sketch, "E3.0.21.4", {"center": v(87.5, 131.25) * mm, "radius": 2.5 * mm});
            skCircle(sketch, "E3.0.21.5", {"center": v(-137.5, 131.25) * mm, "radius": 2.5 * mm});
            skCircle(sketch, "E3.0.21.6", {"center": v(-112.5, 131.25) * mm, "radius": 2.5 * mm});
            skCircle(sketch, "E3.0.21.7", {"center": v(-87.5, 131.25) * mm, "radius": 2.5 * mm});
            skCircle(sketch, "E3.0.21.8", {"center": v(-62.5, 131.25) * mm, "radius": 2.5 * mm});
            skCircle(sketch, "E3.0.21.9", {"center": v(-37.5, 131.25) * mm, "radius": 2.5 * mm});
            skCircle(sketch, "E3.0.21.10", {"center": v(-12.5, 131.25) * mm, "radius": 2.5 * mm});
            skCircle(sketch, "E3.0.21.11", {"center": v(12.5, 131.25) * mm, "radius": 2.5 * mm});
            skCircle(sketch, "E3.0.21.12", {"center": v(162.5, 131.25) * mm, "radius": 2.5 * mm});
            skCircle(sketch, "E3.0.21.13", {"center": v(112.5, 131.25) * mm, "radius": 2.5 * mm});
            skCircle(sketch, "E3.0.21.14", {"center": v(-187.5, 131.25) * mm, "radius": 2.5 * mm});
            skCircle(sketch, "E3.0.21.15", {"center": v(-162.5, 131.25) * mm, "radius": 2.5 * mm});
            skCircle(sketch, "E3.0.22.0", {"center": v(187.5, 156.25) * mm, "radius": 2.5 * mm});
            skCircle(sketch, "E3.0.22.1", {"center": v(37.5, 156.25) * mm, "radius": 2.5 * mm});
            skCircle(sketch, "E3.0.22.2", {"center": v(137.5, 156.25) * mm, "radius": 2.5 * mm});
            skCircle(sketch, "E3.0.22.3", {"center": v(62.5, 156.25) * mm, "radius": 2.5 * mm});
            skCircle(sketch, "E3.0.22.4", {"center": v(87.5, 156.25) * mm, "radius": 2.5 * mm});
            skCircle(sketch, "E3.0.22.5", {"center": v(-137.5, 156.25) * mm, "radius": 2.5 * mm});
            skCircle(sketch, "E3.0.22.6", {"center": v(-112.5, 156.25) * mm, "radius": 2.5 * mm});
            skCircle(sketch, "E3.0.22.7", {"center": v(-87.5, 156.25) * mm, "radius": 2.5 * mm});
            skCircle(sketch, "E3.0.22.8", {"center": v(-62.5, 156.25) * mm, "radius": 2.5 * mm});
            skCircle(sketch, "E3.0.22.9", {"center": v(-37.5, 156.25) * mm, "radius": 2.5 * mm});
            skCircle(sketch, "E3.0.22.10", {"center": v(-12.5, 156.25) * mm, "radius": 2.5 * mm});
            skCircle(sketch, "E3.0.22.11", {"center": v(12.5, 156.25) * mm, "radius": 2.5 * mm});
            skCircle(sketch, "E3.0.22.12", {"center": v(162.5, 156.25) * mm, "radius": 2.5 * mm});
            skCircle(sketch, "E3.0.22.13", {"center": v(112.5, 156.25) * mm, "radius": 2.5 * mm});
            skCircle(sketch, "E3.0.22.14", {"center": v(-187.5, 156.25) * mm, "radius": 2.5 * mm});
            skCircle(sketch, "E3.0.22.15", {"center": v(-162.5, 156.25) * mm, "radius": 2.5 * mm});
            skCircle(sketch, "E3.0.23.0", {"center": v(187.5, 181.25) * mm, "radius": 2.5 * mm});
            skCircle(sketch, "E3.0.23.1", {"center": v(37.5, 181.25) * mm, "radius": 2.5 * mm});
            skCircle(sketch, "E3.0.23.2", {"center": v(137.5, 181.25) * mm, "radius": 2.5 * mm});
            skCircle(sketch, "E3.0.23.3", {"center": v(62.5, 181.25) * mm, "radius": 2.5 * mm});
            skCircle(sketch, "E3.0.23.4", {"center": v(87.5, 181.25) * mm, "radius": 2.5 * mm});
            skCircle(sketch, "E3.0.23.5", {"center": v(-137.5, 181.25) * mm, "radius": 2.5 * mm});
            skCircle(sketch, "E3.0.23.6", {"center": v(-112.5, 181.25) * mm, "radius": 2.5 * mm});
            skCircle(sketch, "E3.0.23.7", {"center": v(-87.5, 181.25) * mm, "radius": 2.5 * mm});
            skCircle(sketch, "E3.0.23.8", {"center": v(-62.5, 181.25) * mm, "radius": 2.5 * mm});
            skCircle(sketch, "E3.0.23.9", {"center": v(-37.5, 181.25) * mm, "radius": 2.5 * mm});
            skCircle(sketch, "E3.0.23.10", {"center": v(-12.5, 181.25) * mm, "radius": 2.5 * mm});
            skCircle(sketch, "E3.0.23.11", {"center": v(12.5, 181.25) * mm, "radius": 2.5 * mm});
            skCircle(sketch, "E3.0.23.12", {"center": v(162.5, 181.25) * mm, "radius": 2.5 * mm});
            skCircle(sketch, "E3.0.23.13", {"center": v(112.5, 181.25) * mm, "radius": 2.5 * mm});
            skCircle(sketch, "E3.0.23.14", {"center": v(-187.5, 181.25) * mm, "radius": 2.5 * mm});
            skCircle(sketch, "E3.0.23.15", {"center": v(-162.5, 181.25) * mm, "radius": 2.5 * mm});
            skCircle(sketch, "E3.0.24.0", {"center": v(187.5, 206.25) * mm, "radius": 2.5 * mm});
            skCircle(sketch, "E3.0.24.1", {"center": v(37.5, 206.25) * mm, "radius": 2.5 * mm});
            skCircle(sketch, "E3.0.24.2", {"center": v(137.5, 206.25) * mm, "radius": 2.5 * mm});
            skCircle(sketch, "E3.0.24.3", {"center": v(62.5, 206.25) * mm, "radius": 2.5 * mm});
            skCircle(sketch, "E3.0.24.4", {"center": v(87.5, 206.25) * mm, "radius": 2.5 * mm});
            skCircle(sketch, "E3.0.24.5", {"center": v(-137.5, 206.25) * mm, "radius": 2.5 * mm});
            skCircle(sketch, "E3.0.24.6", {"center": v(-112.5, 206.25) * mm, "radius": 2.5 * mm});
            skCircle(sketch, "E3.0.24.7", {"center": v(-87.5, 206.25) * mm, "radius": 2.5 * mm});
            skCircle(sketch, "E3.0.24.8", {"center": v(-62.5, 206.25) * mm, "radius": 2.5 * mm});
            skCircle(sketch, "E3.0.24.9", {"center": v(-37.5, 206.25) * mm, "radius": 2.5 * mm});
            skCircle(sketch, "E3.0.24.10", {"center": v(-12.5, 206.25) * mm, "radius": 2.5 * mm});
            skCircle(sketch, "E3.0.24.11", {"center": v(12.5, 206.25) * mm, "radius": 2.5 * mm});
            skCircle(sketch, "E3.0.24.12", {"center": v(162.5, 206.25) * mm, "radius": 2.5 * mm});
            skCircle(sketch, "E3.0.24.13", {"center": v(112.5, 206.25) * mm, "radius": 2.5 * mm});
            skCircle(sketch, "E3.0.24.14", {"center": v(-187.5, 206.25) * mm, "radius": 2.5 * mm});
            skCircle(sketch, "E3.0.24.15", {"center": v(-162.5, 206.25) * mm, "radius": 2.5 * mm});
            skCircle(sketch, "E3.0.25.0", {"center": v(187.5, 231.25) * mm, "radius": 2.5 * mm});
            skCircle(sketch, "E3.0.25.1", {"center": v(37.5, 231.25) * mm, "radius": 2.5 * mm});
            skCircle(sketch, "E3.0.25.2", {"center": v(137.5, 231.25) * mm, "radius": 2.5 * mm});
            skCircle(sketch, "E3.0.25.3", {"center": v(62.5, 231.25) * mm, "radius": 2.5 * mm});
            skCircle(sketch, "E3.0.25.4", {"center": v(87.5, 231.25) * mm, "radius": 2.5 * mm});
            skCircle(sketch, "E3.0.25.5", {"center": v(-137.5, 231.25) * mm, "radius": 2.5 * mm});
            skCircle(sketch, "E3.0.25.6", {"center": v(-112.5, 231.25) * mm, "radius": 2.5 * mm});
            skCircle(sketch, "E3.0.25.7", {"center": v(-87.5, 231.25) * mm, "radius": 2.5 * mm});
            skCircle(sketch, "E3.0.25.8", {"center": v(-62.5, 231.25) * mm, "radius": 2.5 * mm});
            skCircle(sketch, "E3.0.25.9", {"center": v(-37.5, 231.25) * mm, "radius": 2.5 * mm});
            skCircle(sketch, "E3.0.25.10", {"center": v(-12.5, 231.25) * mm, "radius": 2.5 * mm});
            skCircle(sketch, "E3.0.25.11", {"center": v(12.5, 231.25) * mm, "radius": 2.5 * mm});
            skCircle(sketch, "E3.0.25.12", {"center": v(162.5, 231.25) * mm, "radius": 2.5 * mm});
            skCircle(sketch, "E3.0.25.13", {"center": v(112.5, 231.25) * mm, "radius": 2.5 * mm});
            skCircle(sketch, "E3.0.25.14", {"center": v(-187.5, 231.25) * mm, "radius": 2.5 * mm});
            skCircle(sketch, "E3.0.25.15", {"center": v(-162.5, 231.25) * mm, "radius": 2.5 * mm});
            skCircle(sketch, "E3.0.26.0", {"center": v(187.5, 256.25) * mm, "radius": 2.5 * mm});
            skCircle(sketch, "E3.0.26.1", {"center": v(37.5, 256.25) * mm, "radius": 2.5 * mm});
            skCircle(sketch, "E3.0.26.2", {"center": v(137.5, 256.25) * mm, "radius": 2.5 * mm});
            skCircle(sketch, "E3.0.26.3", {"center": v(62.5, 256.25) * mm, "radius": 2.5 * mm});
            skCircle(sketch, "E3.0.26.4", {"center": v(87.5, 256.25) * mm, "radius": 2.5 * mm});
            skCircle(sketch, "E3.0.26.5", {"center": v(-137.5, 256.25) * mm, "radius": 2.5 * mm});
            skCircle(sketch, "E3.0.26.6", {"center": v(-112.5, 256.25) * mm, "radius": 2.5 * mm});
            skCircle(sketch, "E3.0.26.7", {"center": v(-87.5, 256.25) * mm, "radius": 2.5 * mm});
            skCircle(sketch, "E3.0.26.8", {"center": v(-62.5, 256.25) * mm, "radius": 2.5 * mm});
            skCircle(sketch, "E3.0.26.9", {"center": v(-37.5, 256.25) * mm, "radius": 2.5 * mm});
            skCircle(sketch, "E3.0.26.10", {"center": v(-12.5, 256.25) * mm, "radius": 2.5 * mm});
            skCircle(sketch, "E3.0.26.11", {"center": v(12.5, 256.25) * mm, "radius": 2.5 * mm});
            skCircle(sketch, "E3.0.26.12", {"center": v(162.5, 256.25) * mm, "radius": 2.5 * mm});
            skCircle(sketch, "E3.0.26.13", {"center": v(112.5, 256.25) * mm, "radius": 2.5 * mm});
            skCircle(sketch, "E3.0.26.14", {"center": v(-187.5, 256.25) * mm, "radius": 2.5 * mm});
            skCircle(sketch, "E3.0.26.15", {"center": v(-162.5, 256.25) * mm, "radius": 2.5 * mm});
            skCircle(sketch, "E3.0.27.0", {"center": v(187.5, 281.25) * mm, "radius": 2.5 * mm});
            skCircle(sketch, "E3.0.27.1", {"center": v(37.5, 281.25) * mm, "radius": 2.5 * mm});
            skCircle(sketch, "E3.0.27.2", {"center": v(137.5, 281.25) * mm, "radius": 2.5 * mm});
            skCircle(sketch, "E3.0.27.3", {"center": v(62.5, 281.25) * mm, "radius": 2.5 * mm});
            skCircle(sketch, "E3.0.27.4", {"center": v(87.5, 281.25) * mm, "radius": 2.5 * mm});
            skCircle(sketch, "E3.0.27.5", {"center": v(-137.5, 281.25) * mm, "radius": 2.5 * mm});
            skCircle(sketch, "E3.0.27.6", {"center": v(-112.5, 281.25) * mm, "radius": 2.5 * mm});
            skCircle(sketch, "E3.0.27.7", {"center": v(-87.5, 281.25) * mm, "radius": 2.5 * mm});
            skCircle(sketch, "E3.0.27.8", {"center": v(-62.5, 281.25) * mm, "radius": 2.5 * mm});
            skCircle(sketch, "E3.0.27.9", {"center": v(-37.5, 281.25) * mm, "radius": 2.5 * mm});
            skCircle(sketch, "E3.0.27.10", {"center": v(-12.5, 281.25) * mm, "radius": 2.5 * mm});
            skCircle(sketch, "E3.0.27.11", {"center": v(12.5, 281.25) * mm, "radius": 2.5 * mm});
            skCircle(sketch, "E3.0.27.12", {"center": v(162.5, 281.25) * mm, "radius": 2.5 * mm});
            skCircle(sketch, "E3.0.27.13", {"center": v(112.5, 281.25) * mm, "radius": 2.5 * mm});
            skCircle(sketch, "E3.0.27.14", {"center": v(-187.5, 281.25) * mm, "radius": 2.5 * mm});
            skCircle(sketch, "E3.0.27.15", {"center": v(-162.5, 281.25) * mm, "radius": 2.5 * mm});
            skCircle(sketch, "E3.0.28.0", {"center": v(187.5, 306.25) * mm, "radius": 2.5 * mm});
            skCircle(sketch, "E3.0.28.1", {"center": v(37.5, 306.25) * mm, "radius": 2.5 * mm});
            skCircle(sketch, "E3.0.28.2", {"center": v(137.5, 306.25) * mm, "radius": 2.5 * mm});
            skCircle(sketch, "E3.0.28.3", {"center": v(62.5, 306.25) * mm, "radius": 2.5 * mm});
            skCircle(sketch, "E3.0.28.4", {"center": v(87.5, 306.25) * mm, "radius": 2.5 * mm});
            skCircle(sketch, "E3.0.28.5", {"center": v(-137.5, 306.25) * mm, "radius": 2.5 * mm});
            skCircle(sketch, "E3.0.28.6", {"center": v(-112.5, 306.25) * mm, "radius": 2.5 * mm});
            skCircle(sketch, "E3.0.28.7", {"center": v(-87.5, 306.25) * mm, "radius": 2.5 * mm});
            skCircle(sketch, "E3.0.28.8", {"center": v(-62.5, 306.25) * mm, "radius": 2.5 * mm});
            skCircle(sketch, "E3.0.28.9", {"center": v(-37.5, 306.25) * mm, "radius": 2.5 * mm});
            skCircle(sketch, "E3.0.28.10", {"center": v(-12.5, 306.25) * mm, "radius": 2.5 * mm});
            skCircle(sketch, "E3.0.28.11", {"center": v(12.5, 306.25) * mm, "radius": 2.5 * mm});
            skCircle(sketch, "E3.0.28.12", {"center": v(162.5, 306.25) * mm, "radius": 2.5 * mm});
            skCircle(sketch, "E3.0.28.13", {"center": v(112.5, 306.25) * mm, "radius": 2.5 * mm});
            skCircle(sketch, "E3.0.28.14", {"center": v(-187.5, 306.25) * mm, "radius": 2.5 * mm});
            skCircle(sketch, "E3.0.28.15", {"center": v(-162.5, 306.25) * mm, "radius": 2.5 * mm});
            skCircle(sketch, "E3.0.29.0", {"center": v(187.5, 331.25) * mm, "radius": 2.5 * mm});
            skCircle(sketch, "E3.0.29.1", {"center": v(37.5, 331.25) * mm, "radius": 2.5 * mm});
            skCircle(sketch, "E3.0.29.2", {"center": v(137.5, 331.25) * mm, "radius": 2.5 * mm});
            skCircle(sketch, "E3.0.29.3", {"center": v(62.5, 331.25) * mm, "radius": 2.5 * mm});
            skCircle(sketch, "E3.0.29.4", {"center": v(87.5, 331.25) * mm, "radius": 2.5 * mm});
            skCircle(sketch, "E3.0.29.5", {"center": v(-137.5, 331.25) * mm, "radius": 2.5 * mm});
            skCircle(sketch, "E3.0.29.6", {"center": v(-112.5, 331.25) * mm, "radius": 2.5 * mm});
            skCircle(sketch, "E3.0.29.7", {"center": v(-87.5, 331.25) * mm, "radius": 2.5 * mm});
            skCircle(sketch, "E3.0.29.8", {"center": v(-62.5, 331.25) * mm, "radius": 2.5 * mm});
            skCircle(sketch, "E3.0.29.9", {"center": v(-37.5, 331.25) * mm, "radius": 2.5 * mm});
            skCircle(sketch, "E3.0.29.10", {"center": v(-12.5, 331.25) * mm, "radius": 2.5 * mm});
            skCircle(sketch, "E3.0.29.11", {"center": v(12.5, 331.25) * mm, "radius": 2.5 * mm});
            skCircle(sketch, "E3.0.29.12", {"center": v(162.5, 331.25) * mm, "radius": 2.5 * mm});
            skCircle(sketch, "E3.0.29.13", {"center": v(112.5, 331.25) * mm, "radius": 2.5 * mm});
            skCircle(sketch, "E3.0.29.14", {"center": v(-187.5, 331.25) * mm, "radius": 2.5 * mm});
            skCircle(sketch, "E3.0.29.15", {"center": v(-162.5, 331.25) * mm, "radius": 2.5 * mm});
            skCircle(sketch, "E3.0.30.0", {"center": v(187.5, 356.25) * mm, "radius": 2.5 * mm});
            skCircle(sketch, "E3.0.30.1", {"center": v(37.5, 356.25) * mm, "radius": 2.5 * mm});
            skCircle(sketch, "E3.0.30.2", {"center": v(137.5, 356.25) * mm, "radius": 2.5 * mm});
            skCircle(sketch, "E3.0.30.3", {"center": v(62.5, 356.25) * mm, "radius": 2.5 * mm});
            skCircle(sketch, "E3.0.30.4", {"center": v(87.5, 356.25) * mm, "radius": 2.5 * mm});
            skCircle(sketch, "E3.0.30.5", {"center": v(-137.5, 356.25) * mm, "radius": 2.5 * mm});
            skCircle(sketch, "E3.0.30.6", {"center": v(-112.5, 356.25) * mm, "radius": 2.5 * mm});
            skCircle(sketch, "E3.0.30.7", {"center": v(-87.5, 356.25) * mm, "radius": 2.5 * mm});
            skCircle(sketch, "E3.0.30.8", {"center": v(-62.5, 356.25) * mm, "radius": 2.5 * mm});
            skCircle(sketch, "E3.0.30.9", {"center": v(-37.5, 356.25) * mm, "radius": 2.5 * mm});
            skCircle(sketch, "E3.0.30.10", {"center": v(-12.5, 356.25) * mm, "radius": 2.5 * mm});
            skCircle(sketch, "E3.0.30.11", {"center": v(12.5, 356.25) * mm, "radius": 2.5 * mm});
            skCircle(sketch, "E3.0.30.12", {"center": v(162.5, 356.25) * mm, "radius": 2.5 * mm});
            skCircle(sketch, "E3.0.30.13", {"center": v(112.5, 356.25) * mm, "radius": 2.5 * mm});
            skCircle(sketch, "E3.0.30.14", {"center": v(-187.5, 356.25) * mm, "radius": 2.5 * mm});
            skCircle(sketch, "E3.0.30.15", {"center": v(-162.5, 356.25) * mm, "radius": 2.5 * mm});
            skCircle(sketch, "E3.0.31.0", {"center": v(187.5, 381.25) * mm, "radius": 2.5 * mm});
            skCircle(sketch, "E3.0.31.1", {"center": v(37.5, 381.25) * mm, "radius": 2.5 * mm});
            skCircle(sketch, "E3.0.31.2", {"center": v(137.5, 381.25) * mm, "radius": 2.5 * mm});
            skCircle(sketch, "E3.0.31.3", {"center": v(62.5, 381.25) * mm, "radius": 2.5 * mm});
            skCircle(sketch, "E3.0.31.4", {"center": v(87.5, 381.25) * mm, "radius": 2.5 * mm});
            skCircle(sketch, "E3.0.31.5", {"center": v(-137.5, 381.25) * mm, "radius": 2.5 * mm});
            skCircle(sketch, "E3.0.31.6", {"center": v(-112.5, 381.25) * mm, "radius": 2.5 * mm});
            skCircle(sketch, "E3.0.31.7", {"center": v(-87.5, 381.25) * mm, "radius": 2.5 * mm});
            skCircle(sketch, "E3.0.31.8", {"center": v(-62.5, 381.25) * mm, "radius": 2.5 * mm});
            skCircle(sketch, "E3.0.31.9", {"center": v(-37.5, 381.25) * mm, "radius": 2.5 * mm});
            skCircle(sketch, "E3.0.31.10", {"center": v(-12.5, 381.25) * mm, "radius": 2.5 * mm});
            skCircle(sketch, "E3.0.31.11", {"center": v(12.5, 381.25) * mm, "radius": 2.5 * mm});
            skCircle(sketch, "E3.0.31.12", {"center": v(162.5, 381.25) * mm, "radius": 2.5 * mm});
            skCircle(sketch, "E3.0.31.13", {"center": v(112.5, 381.25) * mm, "radius": 2.5 * mm});
            skCircle(sketch, "E3.0.31.14", {"center": v(-187.5, 381.25) * mm, "radius": 2.5 * mm});
            skCircle(sketch, "E3.0.31.15", {"center": v(-162.5, 381.25) * mm, "radius": 2.5 * mm});
            skLineSegment(sketch, "E3.direction2", {"start": v(-187.5, -393.75) * mm, "end": v(-187.5, -368.75) * mm, "construction": true});
            skCircle(sketch, "E4", {"center": v(-187.5, -381.25) * mm, "radius": 2.5 * mm});
            skCircle(sketch, "E5.1.0.0", {"center": v(-172.5, -381.25) * mm, "radius": 2.5 * mm});
            skCircle(sketch, "E5.2.0.0", {"center": v(-157.5, -381.25) * mm, "radius": 2.5 * mm});
            skCircle(sketch, "E5.3.0.0", {"center": v(-142.5, -381.25) * mm, "radius": 2.5 * mm});
            skCircle(sketch, "E5.4.0.0", {"center": v(-127.5, -381.25) * mm, "radius": 2.5 * mm});
            skCircle(sketch, "E5.5.0.0", {"center": v(-112.5, -381.25) * mm, "radius": 2.5 * mm});
            skCircle(sketch, "E5.6.0.0", {"center": v(-97.5, -381.25) * mm, "radius": 2.5 * mm});
            skCircle(sketch, "E5.7.0.0", {"center": v(-82.5, -381.25) * mm, "radius": 2.5 * mm});
            skCircle(sketch, "E5.8.0.0", {"center": v(-67.5, -381.25) * mm, "radius": 2.5 * mm});
            skCircle(sketch, "E5.9.0.0", {"center": v(-52.5, -381.25) * mm, "radius": 2.5 * mm});
            skCircle(sketch, "E5.10.0.0", {"center": v(-37.5, -381.25) * mm, "radius": 2.5 * mm});
            skCircle(sketch, "E5.11.0.0", {"center": v(-22.5, -381.25) * mm, "radius": 2.5 * mm});
            skCircle(sketch, "E5.12.0.0", {"center": v(-7.5, -381.25) * mm, "radius": 2.5 * mm});
            skCircle(sketch, "E5.13.0.0", {"center": v(7.5, -381.25) * mm, "radius": 2.5 * mm});
            skCircle(sketch, "E5.14.0.0", {"center": v(22.5, -381.25) * mm, "radius": 2.5 * mm});
            skCircle(sketch, "E5.15.0.0", {"center": v(37.5, -381.25) * mm, "radius": 2.5 * mm});
            skCircle(sketch, "E5.16.0.0", {"center": v(52.5, -381.25) * mm, "radius": 2.5 * mm});
            skCircle(sketch, "E5.17.0.0", {"center": v(67.5, -381.25) * mm, "radius": 2.5 * mm});
            skCircle(sketch, "E5.18.0.0", {"center": v(82.5, -381.25) * mm, "radius": 2.5 * mm});
            skCircle(sketch, "E5.19.0.0", {"center": v(97.5, -381.25) * mm, "radius": 2.5 * mm});
            skCircle(sketch, "E5.20.0.0", {"center": v(112.5, -381.25) * mm, "radius": 2.5 * mm});
            skCircle(sketch, "E5.21.0.0", {"center": v(127.5, -381.25) * mm, "radius": 2.5 * mm});
            skCircle(sketch, "E5.22.0.0", {"center": v(142.5, -381.25) * mm, "radius": 2.5 * mm});
            skCircle(sketch, "E5.23.0.0", {"center": v(157.5, -381.25) * mm, "radius": 2.5 * mm});
            skCircle(sketch, "E5.24.0.0", {"center": v(172.5, -381.25) * mm, "radius": 2.5 * mm});
            skCircle(sketch, "E5.25.0.0", {"center": v(187.5, -381.25) * mm, "radius": 2.5 * mm});
            skLineSegment(sketch, "E5.direction1", {"start": v(-187.5, -381.25) * mm, "end": v(-172.5, -381.25) * mm, "construction": true});
            skCircle(sketch, "E6.0.1.0", {"center": v(-82.5, -356.25) * mm, "radius": 2.5 * mm});
            skCircle(sketch, "E6.0.1.1", {"center": v(157.5, -356.25) * mm, "radius": 2.5 * mm});
            skCircle(sketch, "E6.0.1.2", {"center": v(-112.5, -356.25) * mm, "radius": 2.5 * mm});
            skCircle(sketch, "E6.0.1.3", {"center": v(127.5, -356.25) * mm, "radius": 2.5 * mm});
            skCircle(sketch, "E6.0.1.4", {"center": v(-127.5, -356.25) * mm, "radius": 2.5 * mm});
            skCircle(sketch, "E6.0.1.5", {"center": v(112.5, -356.25) * mm, "radius": 2.5 * mm});
            skCircle(sketch, "E6.0.1.6", {"center": v(-142.5, -356.25) * mm, "radius": 2.5 * mm});
            skCircle(sketch, "E6.0.1.7", {"center": v(97.5, -356.25) * mm, "radius": 2.5 * mm});
            skCircle(sketch, "E6.0.1.8", {"center": v(-157.5, -356.25) * mm, "radius": 2.5 * mm});
            skCircle(sketch, "E6.0.1.9", {"center": v(82.5, -356.25) * mm, "radius": 2.5 * mm});
            skCircle(sketch, "E6.0.1.10", {"center": v(-172.5, -356.25) * mm, "radius": 2.5 * mm});
            skCircle(sketch, "E6.0.1.11", {"center": v(67.5, -356.25) * mm, "radius": 2.5 * mm});
            skCircle(sketch, "E6.0.1.12", {"center": v(-187.5, -356.25) * mm, "radius": 2.5 * mm});
            skCircle(sketch, "E6.0.1.13", {"center": v(52.5, -356.25) * mm, "radius": 2.5 * mm});
            skCircle(sketch, "E6.0.1.14", {"center": v(37.5, -356.25) * mm, "radius": 2.5 * mm});
            skCircle(sketch, "E6.0.1.15", {"center": v(22.5, -356.25) * mm, "radius": 2.5 * mm});
            skCircle(sketch, "E6.0.1.16", {"center": v(7.5, -356.25) * mm, "radius": 2.5 * mm});
            skCircle(sketch, "E6.0.1.17", {"center": v(-7.5, -356.25) * mm, "radius": 2.5 * mm});
            skCircle(sketch, "E6.0.1.18", {"center": v(-22.5, -356.25) * mm, "radius": 2.5 * mm});
            skCircle(sketch, "E6.0.1.19", {"center": v(-37.5, -356.25) * mm, "radius": 2.5 * mm});
            skLineSegment(sketch, "E6.0.1.20", {"start": v(-187.5, -356.25) * mm, "end": v(-172.5, -356.25) * mm, "construction": true});
            skCircle(sketch, "E6.0.1.21", {"center": v(-52.5, -356.25) * mm, "radius": 2.5 * mm});
            skCircle(sketch, "E6.0.1.22", {"center": v(187.5, -356.25) * mm, "radius": 2.5 * mm});
            skCircle(sketch, "E6.0.1.23", {"center": v(-97.5, -356.25) * mm, "radius": 2.5 * mm});
            skCircle(sketch, "E6.0.1.24", {"center": v(142.5, -356.25) * mm, "radius": 2.5 * mm});
            skCircle(sketch, "E6.0.1.25", {"center": v(-67.5, -356.25) * mm, "radius": 2.5 * mm});
            skCircle(sketch, "E6.0.1.26", {"center": v(172.5, -356.25) * mm, "radius": 2.5 * mm});
            skCircle(sketch, "E6.0.2.0", {"center": v(-82.5, -331.25) * mm, "radius": 2.5 * mm});
            skCircle(sketch, "E6.0.2.1", {"center": v(157.5, -331.25) * mm, "radius": 2.5 * mm});
            skCircle(sketch, "E6.0.2.2", {"center": v(-112.5, -331.25) * mm, "radius": 2.5 * mm});
            skCircle(sketch, "E6.0.2.3", {"center": v(127.5, -331.25) * mm, "radius": 2.5 * mm});
            skCircle(sketch, "E6.0.2.4", {"center": v(-127.5, -331.25) * mm, "radius": 2.5 * mm});
            skCircle(sketch, "E6.0.2.5", {"center": v(112.5, -331.25) * mm, "radius": 2.5 * mm});
            skCircle(sketch, "E6.0.2.6", {"center": v(-142.5, -331.25) * mm, "radius": 2.5 * mm});
            skCircle(sketch, "E6.0.2.7", {"center": v(97.5, -331.25) * mm, "radius": 2.5 * mm});
            skCircle(sketch, "E6.0.2.8", {"center": v(-157.5, -331.25) * mm, "radius": 2.5 * mm});
            skCircle(sketch, "E6.0.2.9", {"center": v(82.5, -331.25) * mm, "radius": 2.5 * mm});
            skCircle(sketch, "E6.0.2.10", {"center": v(-172.5, -331.25) * mm, "radius": 2.5 * mm});
            skCircle(sketch, "E6.0.2.11", {"center": v(67.5, -331.25) * mm, "radius": 2.5 * mm});
            skCircle(sketch, "E6.0.2.12", {"center": v(-187.5, -331.25) * mm, "radius": 2.5 * mm});
            skCircle(sketch, "E6.0.2.13", {"center": v(52.5, -331.25) * mm, "radius": 2.5 * mm});
            skCircle(sketch, "E6.0.2.14", {"center": v(37.5, -331.25) * mm, "radius": 2.5 * mm});
            skCircle(sketch, "E6.0.2.15", {"center": v(22.5, -331.25) * mm, "radius": 2.5 * mm});
            skCircle(sketch, "E6.0.2.16", {"center": v(7.5, -331.25) * mm, "radius": 2.5 * mm});
            skCircle(sketch, "E6.0.2.17", {"center": v(-7.5, -331.25) * mm, "radius": 2.5 * mm});
            skCircle(sketch, "E6.0.2.18", {"center": v(-22.5, -331.25) * mm, "radius": 2.5 * mm});
            skCircle(sketch, "E6.0.2.19", {"center": v(-37.5, -331.25) * mm, "radius": 2.5 * mm});
            skLineSegment(sketch, "E6.0.2.20", {"start": v(-187.5, -331.25) * mm, "end": v(-172.5, -331.25) * mm, "construction": true});
            skCircle(sketch, "E6.0.2.21", {"center": v(-52.5, -331.25) * mm, "radius": 2.5 * mm});
            skCircle(sketch, "E6.0.2.22", {"center": v(187.5, -331.25) * mm, "radius": 2.5 * mm});
            skCircle(sketch, "E6.0.2.23", {"center": v(-97.5, -331.25) * mm, "radius": 2.5 * mm});
            skCircle(sketch, "E6.0.2.24", {"center": v(142.5, -331.25) * mm, "radius": 2.5 * mm});
            skCircle(sketch, "E6.0.2.25", {"center": v(-67.5, -331.25) * mm, "radius": 2.5 * mm});
            skCircle(sketch, "E6.0.2.26", {"center": v(172.5, -331.25) * mm, "radius": 2.5 * mm});
            skCircle(sketch, "E6.0.3.0", {"center": v(-82.5, -306.25) * mm, "radius": 2.5 * mm});
            skCircle(sketch, "E6.0.3.1", {"center": v(157.5, -306.25) * mm, "radius": 2.5 * mm});
            skCircle(sketch, "E6.0.3.2", {"center": v(-112.5, -306.25) * mm, "radius": 2.5 * mm});
            skCircle(sketch, "E6.0.3.3", {"center": v(127.5, -306.25) * mm, "radius": 2.5 * mm});
            skCircle(sketch, "E6.0.3.4", {"center": v(-127.5, -306.25) * mm, "radius": 2.5 * mm});
            skCircle(sketch, "E6.0.3.5", {"center": v(112.5, -306.25) * mm, "radius": 2.5 * mm});
            skCircle(sketch, "E6.0.3.6", {"center": v(-142.5, -306.25) * mm, "radius": 2.5 * mm});
            skCircle(sketch, "E6.0.3.7", {"center": v(97.5, -306.25) * mm, "radius": 2.5 * mm});
            skCircle(sketch, "E6.0.3.8", {"center": v(-157.5, -306.25) * mm, "radius": 2.5 * mm});
            skCircle(sketch, "E6.0.3.9", {"center": v(82.5, -306.25) * mm, "radius": 2.5 * mm});
            skCircle(sketch, "E6.0.3.10", {"center": v(-172.5, -306.25) * mm, "radius": 2.5 * mm});
            skCircle(sketch, "E6.0.3.11", {"center": v(67.5, -306.25) * mm, "radius": 2.5 * mm});
            skCircle(sketch, "E6.0.3.12", {"center": v(-187.5, -306.25) * mm, "radius": 2.5 * mm});
            skCircle(sketch, "E6.0.3.13", {"center": v(52.5, -306.25) * mm, "radius": 2.5 * mm});
            skCircle(sketch, "E6.0.3.14", {"center": v(37.5, -306.25) * mm, "radius": 2.5 * mm});
            skCircle(sketch, "E6.0.3.15", {"center": v(22.5, -306.25) * mm, "radius": 2.5 * mm});
            skCircle(sketch, "E6.0.3.16", {"center": v(7.5, -306.25) * mm, "radius": 2.5 * mm});
            skCircle(sketch, "E6.0.3.17", {"center": v(-7.5, -306.25) * mm, "radius": 2.5 * mm});
            skCircle(sketch, "E6.0.3.18", {"center": v(-22.5, -306.25) * mm, "radius": 2.5 * mm});
            skCircle(sketch, "E6.0.3.19", {"center": v(-37.5, -306.25) * mm, "radius": 2.5 * mm});
            skLineSegment(sketch, "E6.0.3.20", {"start": v(-187.5, -306.25) * mm, "end": v(-172.5, -306.25) * mm, "construction": true});
            skCircle(sketch, "E6.0.3.21", {"center": v(-52.5, -306.25) * mm, "radius": 2.5 * mm});
            skCircle(sketch, "E6.0.3.22", {"center": v(187.5, -306.25) * mm, "radius": 2.5 * mm});
            skCircle(sketch, "E6.0.3.23", {"center": v(-97.5, -306.25) * mm, "radius": 2.5 * mm});
            skCircle(sketch, "E6.0.3.24", {"center": v(142.5, -306.25) * mm, "radius": 2.5 * mm});
            skCircle(sketch, "E6.0.3.25", {"center": v(-67.5, -306.25) * mm, "radius": 2.5 * mm});
            skCircle(sketch, "E6.0.3.26", {"center": v(172.5, -306.25) * mm, "radius": 2.5 * mm});
            skCircle(sketch, "E6.0.4.0", {"center": v(-82.5, -281.25) * mm, "radius": 2.5 * mm});
            skCircle(sketch, "E6.0.4.1", {"center": v(157.5, -281.25) * mm, "radius": 2.5 * mm});
            skCircle(sketch, "E6.0.4.2", {"center": v(-112.5, -281.25) * mm, "radius": 2.5 * mm});
            skCircle(sketch, "E6.0.4.3", {"center": v(127.5, -281.25) * mm, "radius": 2.5 * mm});
            skCircle(sketch, "E6.0.4.4", {"center": v(-127.5, -281.25) * mm, "radius": 2.5 * mm});
            skCircle(sketch, "E6.0.4.5", {"center": v(112.5, -281.25) * mm, "radius": 2.5 * mm});
            skCircle(sketch, "E6.0.4.6", {"center": v(-142.5, -281.25) * mm, "radius": 2.5 * mm});
            skCircle(sketch, "E6.0.4.7", {"center": v(97.5, -281.25) * mm, "radius": 2.5 * mm});
            skCircle(sketch, "E6.0.4.8", {"center": v(-157.5, -281.25) * mm, "radius": 2.5 * mm});
            skCircle(sketch, "E6.0.4.9", {"center": v(82.5, -281.25) * mm, "radius": 2.5 * mm});
            skCircle(sketch, "E6.0.4.10", {"center": v(-172.5, -281.25) * mm, "radius": 2.5 * mm});
            skCircle(sketch, "E6.0.4.11", {"center": v(67.5, -281.25) * mm, "radius": 2.5 * mm});
            skCircle(sketch, "E6.0.4.12", {"center": v(-187.5, -281.25) * mm, "radius": 2.5 * mm});
            skCircle(sketch, "E6.0.4.13", {"center": v(52.5, -281.25) * mm, "radius": 2.5 * mm});
            skCircle(sketch, "E6.0.4.14", {"center": v(37.5, -281.25) * mm, "radius": 2.5 * mm});
            skCircle(sketch, "E6.0.4.15", {"center": v(22.5, -281.25) * mm, "radius": 2.5 * mm});
            skCircle(sketch, "E6.0.4.16", {"center": v(7.5, -281.25) * mm, "radius": 2.5 * mm});
            skCircle(sketch, "E6.0.4.17", {"center": v(-7.5, -281.25) * mm, "radius": 2.5 * mm});
            skCircle(sketch, "E6.0.4.18", {"center": v(-22.5, -281.25) * mm, "radius": 2.5 * mm});
            skCircle(sketch, "E6.0.4.19", {"center": v(-37.5, -281.25) * mm, "radius": 2.5 * mm});
            skLineSegment(sketch, "E6.0.4.20", {"start": v(-187.5, -281.25) * mm, "end": v(-172.5, -281.25) * mm, "construction": true});
            skCircle(sketch, "E6.0.4.21", {"center": v(-52.5, -281.25) * mm, "radius": 2.5 * mm});
            skCircle(sketch, "E6.0.4.22", {"center": v(187.5, -281.25) * mm, "radius": 2.5 * mm});
            skCircle(sketch, "E6.0.4.23", {"center": v(-97.5, -281.25) * mm, "radius": 2.5 * mm});
            skCircle(sketch, "E6.0.4.24", {"center": v(142.5, -281.25) * mm, "radius": 2.5 * mm});
            skCircle(sketch, "E6.0.4.25", {"center": v(-67.5, -281.25) * mm, "radius": 2.5 * mm});
            skCircle(sketch, "E6.0.4.26", {"center": v(172.5, -281.25) * mm, "radius": 2.5 * mm});
            skCircle(sketch, "E6.0.5.0", {"center": v(-82.5, -256.25) * mm, "radius": 2.5 * mm});
            skCircle(sketch, "E6.0.5.1", {"center": v(157.5, -256.25) * mm, "radius": 2.5 * mm});
            skCircle(sketch, "E6.0.5.2", {"center": v(-112.5, -256.25) * mm, "radius": 2.5 * mm});
            skCircle(sketch, "E6.0.5.3", {"center": v(127.5, -256.25) * mm, "radius": 2.5 * mm});
            skCircle(sketch, "E6.0.5.4", {"center": v(-127.5, -256.25) * mm, "radius": 2.5 * mm});
            skCircle(sketch, "E6.0.5.5", {"center": v(112.5, -256.25) * mm, "radius": 2.5 * mm});
            skCircle(sketch, "E6.0.5.6", {"center": v(-142.5, -256.25) * mm, "radius": 2.5 * mm});
            skCircle(sketch, "E6.0.5.7", {"center": v(97.5, -256.25) * mm, "radius": 2.5 * mm});
            skCircle(sketch, "E6.0.5.8", {"center": v(-157.5, -256.25) * mm, "radius": 2.5 * mm});
            skCircle(sketch, "E6.0.5.9", {"center": v(82.5, -256.25) * mm, "radius": 2.5 * mm});
            skCircle(sketch, "E6.0.5.10", {"center": v(-172.5, -256.25) * mm, "radius": 2.5 * mm});
            skCircle(sketch, "E6.0.5.11", {"center": v(67.5, -256.25) * mm, "radius": 2.5 * mm});
            skCircle(sketch, "E6.0.5.12", {"center": v(-187.5, -256.25) * mm, "radius": 2.5 * mm});
            skCircle(sketch, "E6.0.5.13", {"center": v(52.5, -256.25) * mm, "radius": 2.5 * mm});
            skCircle(sketch, "E6.0.5.14", {"center": v(37.5, -256.25) * mm, "radius": 2.5 * mm});
            skCircle(sketch, "E6.0.5.15", {"center": v(22.5, -256.25) * mm, "radius": 2.5 * mm});
            skCircle(sketch, "E6.0.5.16", {"center": v(7.5, -256.25) * mm, "radius": 2.5 * mm});
            skCircle(sketch, "E6.0.5.17", {"center": v(-7.5, -256.25) * mm, "radius": 2.5 * mm});
            skCircle(sketch, "E6.0.5.18", {"center": v(-22.5, -256.25) * mm, "radius": 2.5 * mm});
            skCircle(sketch, "E6.0.5.19", {"center": v(-37.5, -256.25) * mm, "radius": 2.5 * mm});
            skLineSegment(sketch, "E6.0.5.20", {"start": v(-187.5, -256.25) * mm, "end": v(-172.5, -256.25) * mm, "construction": true});
            skCircle(sketch, "E6.0.5.21", {"center": v(-52.5, -256.25) * mm, "radius": 2.5 * mm});
            skCircle(sketch, "E6.0.5.22", {"center": v(187.5, -256.25) * mm, "radius": 2.5 * mm});
            skCircle(sketch, "E6.0.5.23", {"center": v(-97.5, -256.25) * mm, "radius": 2.5 * mm});
            skCircle(sketch, "E6.0.5.24", {"center": v(142.5, -256.25) * mm, "radius": 2.5 * mm});
            skCircle(sketch, "E6.0.5.25", {"center": v(-67.5, -256.25) * mm, "radius": 2.5 * mm});
            skCircle(sketch, "E6.0.5.26", {"center": v(172.5, -256.25) * mm, "radius": 2.5 * mm});
            skCircle(sketch, "E6.0.6.0", {"center": v(-82.5, -231.25) * mm, "radius": 2.5 * mm});
            skCircle(sketch, "E6.0.6.1", {"center": v(157.5, -231.25) * mm, "radius": 2.5 * mm});
            skCircle(sketch, "E6.0.6.2", {"center": v(-112.5, -231.25) * mm, "radius": 2.5 * mm});
            skCircle(sketch, "E6.0.6.3", {"center": v(127.5, -231.25) * mm, "radius": 2.5 * mm});
            skCircle(sketch, "E6.0.6.4", {"center": v(-127.5, -231.25) * mm, "radius": 2.5 * mm});
            skCircle(sketch, "E6.0.6.5", {"center": v(112.5, -231.25) * mm, "radius": 2.5 * mm});
            skCircle(sketch, "E6.0.6.6", {"center": v(-142.5, -231.25) * mm, "radius": 2.5 * mm});
            skCircle(sketch, "E6.0.6.7", {"center": v(97.5, -231.25) * mm, "radius": 2.5 * mm});
            skCircle(sketch, "E6.0.6.8", {"center": v(-157.5, -231.25) * mm, "radius": 2.5 * mm});
            skCircle(sketch, "E6.0.6.9", {"center": v(82.5, -231.25) * mm, "radius": 2.5 * mm});
            skCircle(sketch, "E6.0.6.10", {"center": v(-172.5, -231.25) * mm, "radius": 2.5 * mm});
            skCircle(sketch, "E6.0.6.11", {"center": v(67.5, -231.25) * mm, "radius": 2.5 * mm});
            skCircle(sketch, "E6.0.6.12", {"center": v(-187.5, -231.25) * mm, "radius": 2.5 * mm});
            skCircle(sketch, "E6.0.6.13", {"center": v(52.5, -231.25) * mm, "radius": 2.5 * mm});
            skCircle(sketch, "E6.0.6.14", {"center": v(37.5, -231.25) * mm, "radius": 2.5 * mm});
            skCircle(sketch, "E6.0.6.15", {"center": v(22.5, -231.25) * mm, "radius": 2.5 * mm});
            skCircle(sketch, "E6.0.6.16", {"center": v(7.5, -231.25) * mm, "radius": 2.5 * mm});
            skCircle(sketch, "E6.0.6.17", {"center": v(-7.5, -231.25) * mm, "radius": 2.5 * mm});
            skCircle(sketch, "E6.0.6.18", {"center": v(-22.5, -231.25) * mm, "radius": 2.5 * mm});
            skCircle(sketch, "E6.0.6.19", {"center": v(-37.5, -231.25) * mm, "radius": 2.5 * mm});
            skLineSegment(sketch, "E6.0.6.20", {"start": v(-187.5, -231.25) * mm, "end": v(-172.5, -231.25) * mm, "construction": true});
            skCircle(sketch, "E6.0.6.21", {"center": v(-52.5, -231.25) * mm, "radius": 2.5 * mm});
            skCircle(sketch, "E6.0.6.22", {"center": v(187.5, -231.25) * mm, "radius": 2.5 * mm});
            skCircle(sketch, "E6.0.6.23", {"center": v(-97.5, -231.25) * mm, "radius": 2.5 * mm});
            skCircle(sketch, "E6.0.6.24", {"center": v(142.5, -231.25) * mm, "radius": 2.5 * mm});
            skCircle(sketch, "E6.0.6.25", {"center": v(-67.5, -231.25) * mm, "radius": 2.5 * mm});
            skCircle(sketch, "E6.0.6.26", {"center": v(172.5, -231.25) * mm, "radius": 2.5 * mm});
            skCircle(sketch, "E6.0.7.0", {"center": v(-82.5, -206.25) * mm, "radius": 2.5 * mm});
            skCircle(sketch, "E6.0.7.1", {"center": v(157.5, -206.25) * mm, "radius": 2.5 * mm});
            skCircle(sketch, "E6.0.7.2", {"center": v(-112.5, -206.25) * mm, "radius": 2.5 * mm});
            skCircle(sketch, "E6.0.7.3", {"center": v(127.5, -206.25) * mm, "radius": 2.5 * mm});
            skCircle(sketch, "E6.0.7.4", {"center": v(-127.5, -206.25) * mm, "radius": 2.5 * mm});
            skCircle(sketch, "E6.0.7.5", {"center": v(112.5, -206.25) * mm, "radius": 2.5 * mm});
            skCircle(sketch, "E6.0.7.6", {"center": v(-142.5, -206.25) * mm, "radius": 2.5 * mm});
            skCircle(sketch, "E6.0.7.7", {"center": v(97.5, -206.25) * mm, "radius": 2.5 * mm});
            skCircle(sketch, "E6.0.7.8", {"center": v(-157.5, -206.25) * mm, "radius": 2.5 * mm});
            skCircle(sketch, "E6.0.7.9", {"center": v(82.5, -206.25) * mm, "radius": 2.5 * mm});
            skCircle(sketch, "E6.0.7.10", {"center": v(-172.5, -206.25) * mm, "radius": 2.5 * mm});
            skCircle(sketch, "E6.0.7.11", {"center": v(67.5, -206.25) * mm, "radius": 2.5 * mm});
            skCircle(sketch, "E6.0.7.12", {"center": v(-187.5, -206.25) * mm, "radius": 2.5 * mm});
            skCircle(sketch, "E6.0.7.13", {"center": v(52.5, -206.25) * mm, "radius": 2.5 * mm});
            skCircle(sketch, "E6.0.7.14", {"center": v(37.5, -206.25) * mm, "radius": 2.5 * mm});
            skCircle(sketch, "E6.0.7.15", {"center": v(22.5, -206.25) * mm, "radius": 2.5 * mm});
            skCircle(sketch, "E6.0.7.16", {"center": v(7.5, -206.25) * mm, "radius": 2.5 * mm});
            skCircle(sketch, "E6.0.7.17", {"center": v(-7.5, -206.25) * mm, "radius": 2.5 * mm});
            skCircle(sketch, "E6.0.7.18", {"center": v(-22.5, -206.25) * mm, "radius": 2.5 * mm});
            skCircle(sketch, "E6.0.7.19", {"center": v(-37.5, -206.25) * mm, "radius": 2.5 * mm});
            skLineSegment(sketch, "E6.0.7.20", {"start": v(-187.5, -206.25) * mm, "end": v(-172.5, -206.25) * mm, "construction": true});
            skCircle(sketch, "E6.0.7.21", {"center": v(-52.5, -206.25) * mm, "radius": 2.5 * mm});
            skCircle(sketch, "E6.0.7.22", {"center": v(187.5, -206.25) * mm, "radius": 2.5 * mm});
            skCircle(sketch, "E6.0.7.23", {"center": v(-97.5, -206.25) * mm, "radius": 2.5 * mm});
            skCircle(sketch, "E6.0.7.24", {"center": v(142.5, -206.25) * mm, "radius": 2.5 * mm});
            skCircle(sketch, "E6.0.7.25", {"center": v(-67.5, -206.25) * mm, "radius": 2.5 * mm});
            skCircle(sketch, "E6.0.7.26", {"center": v(172.5, -206.25) * mm, "radius": 2.5 * mm});
            skCircle(sketch, "E6.0.8.0", {"center": v(-82.5, -181.25) * mm, "radius": 2.5 * mm});
            skCircle(sketch, "E6.0.8.1", {"center": v(157.5, -181.25) * mm, "radius": 2.5 * mm});
            skCircle(sketch, "E6.0.8.2", {"center": v(-112.5, -181.25) * mm, "radius": 2.5 * mm});
            skCircle(sketch, "E6.0.8.3", {"center": v(127.5, -181.25) * mm, "radius": 2.5 * mm});
            skCircle(sketch, "E6.0.8.4", {"center": v(-127.5, -181.25) * mm, "radius": 2.5 * mm});
            skCircle(sketch, "E6.0.8.5", {"center": v(112.5, -181.25) * mm, "radius": 2.5 * mm});
            skCircle(sketch, "E6.0.8.6", {"center": v(-142.5, -181.25) * mm, "radius": 2.5 * mm});
            skCircle(sketch, "E6.0.8.7", {"center": v(97.5, -181.25) * mm, "radius": 2.5 * mm});
            skCircle(sketch, "E6.0.8.8", {"center": v(-157.5, -181.25) * mm, "radius": 2.5 * mm});
            skCircle(sketch, "E6.0.8.9", {"center": v(82.5, -181.25) * mm, "radius": 2.5 * mm});
            skCircle(sketch, "E6.0.8.10", {"center": v(-172.5, -181.25) * mm, "radius": 2.5 * mm});
            skCircle(sketch, "E6.0.8.11", {"center": v(67.5, -181.25) * mm, "radius": 2.5 * mm});
            skCircle(sketch, "E6.0.8.12", {"center": v(-187.5, -181.25) * mm, "radius": 2.5 * mm});
            skCircle(sketch, "E6.0.8.13", {"center": v(52.5, -181.25) * mm, "radius": 2.5 * mm});
            skCircle(sketch, "E6.0.8.14", {"center": v(37.5, -181.25) * mm, "radius": 2.5 * mm});
            skCircle(sketch, "E6.0.8.15", {"center": v(22.5, -181.25) * mm, "radius": 2.5 * mm});
            skCircle(sketch, "E6.0.8.16", {"center": v(7.5, -181.25) * mm, "radius": 2.5 * mm});
            skCircle(sketch, "E6.0.8.17", {"center": v(-7.5, -181.25) * mm, "radius": 2.5 * mm});
            skCircle(sketch, "E6.0.8.18", {"center": v(-22.5, -181.25) * mm, "radius": 2.5 * mm});
            skCircle(sketch, "E6.0.8.19", {"center": v(-37.5, -181.25) * mm, "radius": 2.5 * mm});
            skLineSegment(sketch, "E6.0.8.20", {"start": v(-187.5, -181.25) * mm, "end": v(-172.5, -181.25) * mm, "construction": true});
            skCircle(sketch, "E6.0.8.21", {"center": v(-52.5, -181.25) * mm, "radius": 2.5 * mm});
            skCircle(sketch, "E6.0.8.22", {"center": v(187.5, -181.25) * mm, "radius": 2.5 * mm});
            skCircle(sketch, "E6.0.8.23", {"center": v(-97.5, -181.25) * mm, "radius": 2.5 * mm});
            skCircle(sketch, "E6.0.8.24", {"center": v(142.5, -181.25) * mm, "radius": 2.5 * mm});
            skCircle(sketch, "E6.0.8.25", {"center": v(-67.5, -181.25) * mm, "radius": 2.5 * mm});
            skCircle(sketch, "E6.0.8.26", {"center": v(172.5, -181.25) * mm, "radius": 2.5 * mm});
            skCircle(sketch, "E6.0.9.0", {"center": v(-82.5, -156.25) * mm, "radius": 2.5 * mm});
            skCircle(sketch, "E6.0.9.1", {"center": v(157.5, -156.25) * mm, "radius": 2.5 * mm});
            skCircle(sketch, "E6.0.9.2", {"center": v(-112.5, -156.25) * mm, "radius": 2.5 * mm});
            skCircle(sketch, "E6.0.9.3", {"center": v(127.5, -156.25) * mm, "radius": 2.5 * mm});
            skCircle(sketch, "E6.0.9.4", {"center": v(-127.5, -156.25) * mm, "radius": 2.5 * mm});
            skCircle(sketch, "E6.0.9.5", {"center": v(112.5, -156.25) * mm, "radius": 2.5 * mm});
            skCircle(sketch, "E6.0.9.6", {"center": v(-142.5, -156.25) * mm, "radius": 2.5 * mm});
            skCircle(sketch, "E6.0.9.7", {"center": v(97.5, -156.25) * mm, "radius": 2.5 * mm});
            skCircle(sketch, "E6.0.9.8", {"center": v(-157.5, -156.25) * mm, "radius": 2.5 * mm});
            skCircle(sketch, "E6.0.9.9", {"center": v(82.5, -156.25) * mm, "radius": 2.5 * mm});
            skCircle(sketch, "E6.0.9.10", {"center": v(-172.5, -156.25) * mm, "radius": 2.5 * mm});
            skCircle(sketch, "E6.0.9.11", {"center": v(67.5, -156.25) * mm, "radius": 2.5 * mm});
            skCircle(sketch, "E6.0.9.12", {"center": v(-187.5, -156.25) * mm, "radius": 2.5 * mm});
            skCircle(sketch, "E6.0.9.13", {"center": v(52.5, -156.25) * mm, "radius": 2.5 * mm});
            skCircle(sketch, "E6.0.9.14", {"center": v(37.5, -156.25) * mm, "radius": 2.5 * mm});
            skCircle(sketch, "E6.0.9.15", {"center": v(22.5, -156.25) * mm, "radius": 2.5 * mm});
            skCircle(sketch, "E6.0.9.16", {"center": v(7.5, -156.25) * mm, "radius": 2.5 * mm});
            skCircle(sketch, "E6.0.9.17", {"center": v(-7.5, -156.25) * mm, "radius": 2.5 * mm});
            skCircle(sketch, "E6.0.9.18", {"center": v(-22.5, -156.25) * mm, "radius": 2.5 * mm});
            skCircle(sketch, "E6.0.9.19", {"center": v(-37.5, -156.25) * mm, "radius": 2.5 * mm});
            skLineSegment(sketch, "E6.0.9.20", {"start": v(-187.5, -156.25) * mm, "end": v(-172.5, -156.25) * mm, "construction": true});
            skCircle(sketch, "E6.0.9.21", {"center": v(-52.5, -156.25) * mm, "radius": 2.5 * mm});
            skCircle(sketch, "E6.0.9.22", {"center": v(187.5, -156.25) * mm, "radius": 2.5 * mm});
            skCircle(sketch, "E6.0.9.23", {"center": v(-97.5, -156.25) * mm, "radius": 2.5 * mm});
            skCircle(sketch, "E6.0.9.24", {"center": v(142.5, -156.25) * mm, "radius": 2.5 * mm});
            skCircle(sketch, "E6.0.9.25", {"center": v(-67.5, -156.25) * mm, "radius": 2.5 * mm});
            skCircle(sketch, "E6.0.9.26", {"center": v(172.5, -156.25) * mm, "radius": 2.5 * mm});
            skCircle(sketch, "E6.0.10.0", {"center": v(-82.5, -131.25) * mm, "radius": 2.5 * mm});
            skCircle(sketch, "E6.0.10.1", {"center": v(157.5, -131.25) * mm, "radius": 2.5 * mm});
            skCircle(sketch, "E6.0.10.2", {"center": v(-112.5, -131.25) * mm, "radius": 2.5 * mm});
            skCircle(sketch, "E6.0.10.3", {"center": v(127.5, -131.25) * mm, "radius": 2.5 * mm});
            skCircle(sketch, "E6.0.10.4", {"center": v(-127.5, -131.25) * mm, "radius": 2.5 * mm});
            skCircle(sketch, "E6.0.10.5", {"center": v(112.5, -131.25) * mm, "radius": 2.5 * mm});
            skCircle(sketch, "E6.0.10.6", {"center": v(-142.5, -131.25) * mm, "radius": 2.5 * mm});
            skCircle(sketch, "E6.0.10.7", {"center": v(97.5, -131.25) * mm, "radius": 2.5 * mm});
            skCircle(sketch, "E6.0.10.8", {"center": v(-157.5, -131.25) * mm, "radius": 2.5 * mm});
            skCircle(sketch, "E6.0.10.9", {"center": v(82.5, -131.25) * mm, "radius": 2.5 * mm});
            skCircle(sketch, "E6.0.10.10", {"center": v(-172.5, -131.25) * mm, "radius": 2.5 * mm});
            skCircle(sketch, "E6.0.10.11", {"center": v(67.5, -131.25) * mm, "radius": 2.5 * mm});
            skCircle(sketch, "E6.0.10.12", {"center": v(-187.5, -131.25) * mm, "radius": 2.5 * mm});
            skCircle(sketch, "E6.0.10.13", {"center": v(52.5, -131.25) * mm, "radius": 2.5 * mm});
            skCircle(sketch, "E6.0.10.14", {"center": v(37.5, -131.25) * mm, "radius": 2.5 * mm});
            skCircle(sketch, "E6.0.10.15", {"center": v(22.5, -131.25) * mm, "radius": 2.5 * mm});
            skCircle(sketch, "E6.0.10.16", {"center": v(7.5, -131.25) * mm, "radius": 2.5 * mm});
            skCircle(sketch, "E6.0.10.17", {"center": v(-7.5, -131.25) * mm, "radius": 2.5 * mm});
            skCircle(sketch, "E6.0.10.18", {"center": v(-22.5, -131.25) * mm, "radius": 2.5 * mm});
            skCircle(sketch, "E6.0.10.19", {"center": v(-37.5, -131.25) * mm, "radius": 2.5 * mm});
            skLineSegment(sketch, "E6.0.10.20", {"start": v(-187.5, -131.25) * mm, "end": v(-172.5, -131.25) * mm, "construction": true});
            skCircle(sketch, "E6.0.10.21", {"center": v(-52.5, -131.25) * mm, "radius": 2.5 * mm});
            skCircle(sketch, "E6.0.10.22", {"center": v(187.5, -131.25) * mm, "radius": 2.5 * mm});
            skCircle(sketch, "E6.0.10.23", {"center": v(-97.5, -131.25) * mm, "radius": 2.5 * mm});
            skCircle(sketch, "E6.0.10.24", {"center": v(142.5, -131.25) * mm, "radius": 2.5 * mm});
            skCircle(sketch, "E6.0.10.25", {"center": v(-67.5, -131.25) * mm, "radius": 2.5 * mm});
            skCircle(sketch, "E6.0.10.26", {"center": v(172.5, -131.25) * mm, "radius": 2.5 * mm});
            skCircle(sketch, "E6.0.11.0", {"center": v(-82.5, -106.25) * mm, "radius": 2.5 * mm});
            skCircle(sketch, "E6.0.11.1", {"center": v(157.5, -106.25) * mm, "radius": 2.5 * mm});
            skCircle(sketch, "E6.0.11.2", {"center": v(-112.5, -106.25) * mm, "radius": 2.5 * mm});
            skCircle(sketch, "E6.0.11.3", {"center": v(127.5, -106.25) * mm, "radius": 2.5 * mm});
            skCircle(sketch, "E6.0.11.4", {"center": v(-127.5, -106.25) * mm, "radius": 2.5 * mm});
            skCircle(sketch, "E6.0.11.5", {"center": v(112.5, -106.25) * mm, "radius": 2.5 * mm});
            skCircle(sketch, "E6.0.11.6", {"center": v(-142.5, -106.25) * mm, "radius": 2.5 * mm});
            skCircle(sketch, "E6.0.11.7", {"center": v(97.5, -106.25) * mm, "radius": 2.5 * mm});
            skCircle(sketch, "E6.0.11.8", {"center": v(-157.5, -106.25) * mm, "radius": 2.5 * mm});
            skCircle(sketch, "E6.0.11.9", {"center": v(82.5, -106.25) * mm, "radius": 2.5 * mm});
            skCircle(sketch, "E6.0.11.10", {"center": v(-172.5, -106.25) * mm, "radius": 2.5 * mm});
            skCircle(sketch, "E6.0.11.11", {"center": v(67.5, -106.25) * mm, "radius": 2.5 * mm});
            skCircle(sketch, "E6.0.11.12", {"center": v(-187.5, -106.25) * mm, "radius": 2.5 * mm});
            skCircle(sketch, "E6.0.11.13", {"center": v(52.5, -106.25) * mm, "radius": 2.5 * mm});
            skCircle(sketch, "E6.0.11.14", {"center": v(37.5, -106.25) * mm, "radius": 2.5 * mm});
            skCircle(sketch, "E6.0.11.15", {"center": v(22.5, -106.25) * mm, "radius": 2.5 * mm});
            skCircle(sketch, "E6.0.11.16", {"center": v(7.5, -106.25) * mm, "radius": 2.5 * mm});
            skCircle(sketch, "E6.0.11.17", {"center": v(-7.5, -106.25) * mm, "radius": 2.5 * mm});
            skCircle(sketch, "E6.0.11.18", {"center": v(-22.5, -106.25) * mm, "radius": 2.5 * mm});
            skCircle(sketch, "E6.0.11.19", {"center": v(-37.5, -106.25) * mm, "radius": 2.5 * mm});
            skLineSegment(sketch, "E6.0.11.20", {"start": v(-187.5, -106.25) * mm, "end": v(-172.5, -106.25) * mm, "construction": true});
            skCircle(sketch, "E6.0.11.21", {"center": v(-52.5, -106.25) * mm, "radius": 2.5 * mm});
            skCircle(sketch, "E6.0.11.22", {"center": v(187.5, -106.25) * mm, "radius": 2.5 * mm});
            skCircle(sketch, "E6.0.11.23", {"center": v(-97.5, -106.25) * mm, "radius": 2.5 * mm});
            skCircle(sketch, "E6.0.11.24", {"center": v(142.5, -106.25) * mm, "radius": 2.5 * mm});
            skCircle(sketch, "E6.0.11.25", {"center": v(-67.5, -106.25) * mm, "radius": 2.5 * mm});
            skCircle(sketch, "E6.0.11.26", {"center": v(172.5, -106.25) * mm, "radius": 2.5 * mm});
            skCircle(sketch, "E6.0.12.0", {"center": v(-82.5, -81.25) * mm, "radius": 2.5 * mm});
            skCircle(sketch, "E6.0.12.1", {"center": v(157.5, -81.25) * mm, "radius": 2.5 * mm});
            skCircle(sketch, "E6.0.12.2", {"center": v(-112.5, -81.25) * mm, "radius": 2.5 * mm});
            skCircle(sketch, "E6.0.12.3", {"center": v(127.5, -81.25) * mm, "radius": 2.5 * mm});
            skCircle(sketch, "E6.0.12.4", {"center": v(-127.5, -81.25) * mm, "radius": 2.5 * mm});
            skCircle(sketch, "E6.0.12.5", {"center": v(112.5, -81.25) * mm, "radius": 2.5 * mm});
            skCircle(sketch, "E6.0.12.6", {"center": v(-142.5, -81.25) * mm, "radius": 2.5 * mm});
            skCircle(sketch, "E6.0.12.7", {"center": v(97.5, -81.25) * mm, "radius": 2.5 * mm});
            skCircle(sketch, "E6.0.12.8", {"center": v(-157.5, -81.25) * mm, "radius": 2.5 * mm});
            skCircle(sketch, "E6.0.12.9", {"center": v(82.5, -81.25) * mm, "radius": 2.5 * mm});
            skCircle(sketch, "E6.0.12.10", {"center": v(-172.5, -81.25) * mm, "radius": 2.5 * mm});
            skCircle(sketch, "E6.0.12.11", {"center": v(67.5, -81.25) * mm, "radius": 2.5 * mm});
            skCircle(sketch, "E6.0.12.12", {"center": v(-187.5, -81.25) * mm, "radius": 2.5 * mm});
            skCircle(sketch, "E6.0.12.13", {"center": v(52.5, -81.25) * mm, "radius": 2.5 * mm});
            skCircle(sketch, "E6.0.12.14", {"center": v(37.5, -81.25) * mm, "radius": 2.5 * mm});
            skCircle(sketch, "E6.0.12.15", {"center": v(22.5, -81.25) * mm, "radius": 2.5 * mm});
            skCircle(sketch, "E6.0.12.16", {"center": v(7.5, -81.25) * mm, "radius": 2.5 * mm});
            skCircle(sketch, "E6.0.12.17", {"center": v(-7.5, -81.25) * mm, "radius": 2.5 * mm});
            skCircle(sketch, "E6.0.12.18", {"center": v(-22.5, -81.25) * mm, "radius": 2.5 * mm});
            skCircle(sketch, "E6.0.12.19", {"center": v(-37.5, -81.25) * mm, "radius": 2.5 * mm});
            skLineSegment(sketch, "E6.0.12.20", {"start": v(-187.5, -81.25) * mm, "end": v(-172.5, -81.25) * mm, "construction": true});
            skCircle(sketch, "E6.0.12.21", {"center": v(-52.5, -81.25) * mm, "radius": 2.5 * mm});
            skCircle(sketch, "E6.0.12.22", {"center": v(187.5, -81.25) * mm, "radius": 2.5 * mm});
            skCircle(sketch, "E6.0.12.23", {"center": v(-97.5, -81.25) * mm, "radius": 2.5 * mm});
            skCircle(sketch, "E6.0.12.24", {"center": v(142.5, -81.25) * mm, "radius": 2.5 * mm});
            skCircle(sketch, "E6.0.12.25", {"center": v(-67.5, -81.25) * mm, "radius": 2.5 * mm});
            skCircle(sketch, "E6.0.12.26", {"center": v(172.5, -81.25) * mm, "radius": 2.5 * mm});
            skCircle(sketch, "E6.0.13.0", {"center": v(-82.5, -56.25) * mm, "radius": 2.5 * mm});
            skCircle(sketch, "E6.0.13.1", {"center": v(157.5, -56.25) * mm, "radius": 2.5 * mm});
            skCircle(sketch, "E6.0.13.2", {"center": v(-112.5, -56.25) * mm, "radius": 2.5 * mm});
            skCircle(sketch, "E6.0.13.3", {"center": v(127.5, -56.25) * mm, "radius": 2.5 * mm});
            skCircle(sketch, "E6.0.13.4", {"center": v(-127.5, -56.25) * mm, "radius": 2.5 * mm});
            skCircle(sketch, "E6.0.13.5", {"center": v(112.5, -56.25) * mm, "radius": 2.5 * mm});
            skCircle(sketch, "E6.0.13.6", {"center": v(-142.5, -56.25) * mm, "radius": 2.5 * mm});
            skCircle(sketch, "E6.0.13.7", {"center": v(97.5, -56.25) * mm, "radius": 2.5 * mm});
            skCircle(sketch, "E6.0.13.8", {"center": v(-157.5, -56.25) * mm, "radius": 2.5 * mm});
            skCircle(sketch, "E6.0.13.9", {"center": v(82.5, -56.25) * mm, "radius": 2.5 * mm});
            skCircle(sketch, "E6.0.13.10", {"center": v(-172.5, -56.25) * mm, "radius": 2.5 * mm});
            skCircle(sketch, "E6.0.13.11", {"center": v(67.5, -56.25) * mm, "radius": 2.5 * mm});
            skCircle(sketch, "E6.0.13.12", {"center": v(-187.5, -56.25) * mm, "radius": 2.5 * mm});
            skCircle(sketch, "E6.0.13.13", {"center": v(52.5, -56.25) * mm, "radius": 2.5 * mm});
            skCircle(sketch, "E6.0.13.14", {"center": v(37.5, -56.25) * mm, "radius": 2.5 * mm});
            skCircle(sketch, "E6.0.13.15", {"center": v(22.5, -56.25) * mm, "radius": 2.5 * mm});
            skCircle(sketch, "E6.0.13.16", {"center": v(7.5, -56.25) * mm, "radius": 2.5 * mm});
            skCircle(sketch, "E6.0.13.17", {"center": v(-7.5, -56.25) * mm, "radius": 2.5 * mm});
            skCircle(sketch, "E6.0.13.18", {"center": v(-22.5, -56.25) * mm, "radius": 2.5 * mm});
            skCircle(sketch, "E6.0.13.19", {"center": v(-37.5, -56.25) * mm, "radius": 2.5 * mm});
            skLineSegment(sketch, "E6.0.13.20", {"start": v(-187.5, -56.25) * mm, "end": v(-172.5, -56.25) * mm, "construction": true});
            skCircle(sketch, "E6.0.13.21", {"center": v(-52.5, -56.25) * mm, "radius": 2.5 * mm});
            skCircle(sketch, "E6.0.13.22", {"center": v(187.5, -56.25) * mm, "radius": 2.5 * mm});
            skCircle(sketch, "E6.0.13.23", {"center": v(-97.5, -56.25) * mm, "radius": 2.5 * mm});
            skCircle(sketch, "E6.0.13.24", {"center": v(142.5, -56.25) * mm, "radius": 2.5 * mm});
            skCircle(sketch, "E6.0.13.25", {"center": v(-67.5, -56.25) * mm, "radius": 2.5 * mm});
            skCircle(sketch, "E6.0.13.26", {"center": v(172.5, -56.25) * mm, "radius": 2.5 * mm});
            skCircle(sketch, "E6.0.14.0", {"center": v(-82.5, -31.25) * mm, "radius": 2.5 * mm});
            skCircle(sketch, "E6.0.14.1", {"center": v(157.5, -31.25) * mm, "radius": 2.5 * mm});
            skCircle(sketch, "E6.0.14.2", {"center": v(-112.5, -31.25) * mm, "radius": 2.5 * mm});
            skCircle(sketch, "E6.0.14.3", {"center": v(127.5, -31.25) * mm, "radius": 2.5 * mm});
            skCircle(sketch, "E6.0.14.4", {"center": v(-127.5, -31.25) * mm, "radius": 2.5 * mm});
            skCircle(sketch, "E6.0.14.5", {"center": v(112.5, -31.25) * mm, "radius": 2.5 * mm});
            skCircle(sketch, "E6.0.14.6", {"center": v(-142.5, -31.25) * mm, "radius": 2.5 * mm});
            skCircle(sketch, "E6.0.14.7", {"center": v(97.5, -31.25) * mm, "radius": 2.5 * mm});
            skCircle(sketch, "E6.0.14.8", {"center": v(-157.5, -31.25) * mm, "radius": 2.5 * mm});
            skCircle(sketch, "E6.0.14.9", {"center": v(82.5, -31.25) * mm, "radius": 2.5 * mm});
            skCircle(sketch, "E6.0.14.10", {"center": v(-172.5, -31.25) * mm, "radius": 2.5 * mm});
            skCircle(sketch, "E6.0.14.11", {"center": v(67.5, -31.25) * mm, "radius": 2.5 * mm});
            skCircle(sketch, "E6.0.14.12", {"center": v(-187.5, -31.25) * mm, "radius": 2.5 * mm});
            skCircle(sketch, "E6.0.14.13", {"center": v(52.5, -31.25) * mm, "radius": 2.5 * mm});
            skCircle(sketch, "E6.0.14.14", {"center": v(37.5, -31.25) * mm, "radius": 2.5 * mm});
            skCircle(sketch, "E6.0.14.15", {"center": v(22.5, -31.25) * mm, "radius": 2.5 * mm});
            skCircle(sketch, "E6.0.14.16", {"center": v(7.5, -31.25) * mm, "radius": 2.5 * mm});
            skCircle(sketch, "E6.0.14.17", {"center": v(-7.5, -31.25) * mm, "radius": 2.5 * mm});
            skCircle(sketch, "E6.0.14.18", {"center": v(-22.5, -31.25) * mm, "radius": 2.5 * mm});
            skCircle(sketch, "E6.0.14.19", {"center": v(-37.5, -31.25) * mm, "radius": 2.5 * mm});
            skLineSegment(sketch, "E6.0.14.20", {"start": v(-187.5, -31.25) * mm, "end": v(-172.5, -31.25) * mm, "construction": true});
            skCircle(sketch, "E6.0.14.21", {"center": v(-52.5, -31.25) * mm, "radius": 2.5 * mm});
            skCircle(sketch, "E6.0.14.22", {"center": v(187.5, -31.25) * mm, "radius": 2.5 * mm});
            skCircle(sketch, "E6.0.14.23", {"center": v(-97.5, -31.25) * mm, "radius": 2.5 * mm});
            skCircle(sketch, "E6.0.14.24", {"center": v(142.5, -31.25) * mm, "radius": 2.5 * mm});
            skCircle(sketch, "E6.0.14.25", {"center": v(-67.5, -31.25) * mm, "radius": 2.5 * mm});
            skCircle(sketch, "E6.0.14.26", {"center": v(172.5, -31.25) * mm, "radius": 2.5 * mm});
            skCircle(sketch, "E6.0.15.0", {"center": v(-82.5, -6.25) * mm, "radius": 2.5 * mm});
            skCircle(sketch, "E6.0.15.1", {"center": v(157.5, -6.25) * mm, "radius": 2.5 * mm});
            skCircle(sketch, "E6.0.15.2", {"center": v(-112.5, -6.25) * mm, "radius": 2.5 * mm});
            skCircle(sketch, "E6.0.15.3", {"center": v(127.5, -6.25) * mm, "radius": 2.5 * mm});
            skCircle(sketch, "E6.0.15.4", {"center": v(-127.5, -6.25) * mm, "radius": 2.5 * mm});
            skCircle(sketch, "E6.0.15.5", {"center": v(112.5, -6.25) * mm, "radius": 2.5 * mm});
            skCircle(sketch, "E6.0.15.6", {"center": v(-142.5, -6.25) * mm, "radius": 2.5 * mm});
            skCircle(sketch, "E6.0.15.7", {"center": v(97.5, -6.25) * mm, "radius": 2.5 * mm});
            skCircle(sketch, "E6.0.15.8", {"center": v(-157.5, -6.25) * mm, "radius": 2.5 * mm});
            skCircle(sketch, "E6.0.15.9", {"center": v(82.5, -6.25) * mm, "radius": 2.5 * mm});
            skCircle(sketch, "E6.0.15.10", {"center": v(-172.5, -6.25) * mm, "radius": 2.5 * mm});
            skCircle(sketch, "E6.0.15.11", {"center": v(67.5, -6.25) * mm, "radius": 2.5 * mm});
            skCircle(sketch, "E6.0.15.12", {"center": v(-187.5, -6.25) * mm, "radius": 2.5 * mm});
            skCircle(sketch, "E6.0.15.13", {"center": v(52.5, -6.25) * mm, "radius": 2.5 * mm});
            skCircle(sketch, "E6.0.15.14", {"center": v(37.5, -6.25) * mm, "radius": 2.5 * mm});
            skCircle(sketch, "E6.0.15.15", {"center": v(22.5, -6.25) * mm, "radius": 2.5 * mm});
            skCircle(sketch, "E6.0.15.16", {"center": v(7.5, -6.25) * mm, "radius": 2.5 * mm});
            skCircle(sketch, "E6.0.15.17", {"center": v(-7.5, -6.25) * mm, "radius": 2.5 * mm});
            skCircle(sketch, "E6.0.15.18", {"center": v(-22.5, -6.25) * mm, "radius": 2.5 * mm});
            skCircle(sketch, "E6.0.15.19", {"center": v(-37.5, -6.25) * mm, "radius": 2.5 * mm});
            skLineSegment(sketch, "E6.0.15.20", {"start": v(-187.5, -6.25) * mm, "end": v(-172.5, -6.25) * mm, "construction": true});
            skCircle(sketch, "E6.0.15.21", {"center": v(-52.5, -6.25) * mm, "radius": 2.5 * mm});
            skCircle(sketch, "E6.0.15.22", {"center": v(187.5, -6.25) * mm, "radius": 2.5 * mm});
            skCircle(sketch, "E6.0.15.23", {"center": v(-97.5, -6.25) * mm, "radius": 2.5 * mm});
            skCircle(sketch, "E6.0.15.24", {"center": v(142.5, -6.25) * mm, "radius": 2.5 * mm});
            skCircle(sketch, "E6.0.15.25", {"center": v(-67.5, -6.25) * mm, "radius": 2.5 * mm});
            skCircle(sketch, "E6.0.15.26", {"center": v(172.5, -6.25) * mm, "radius": 2.5 * mm});
            skCircle(sketch, "E6.0.16.0", {"center": v(-82.5, 18.75) * mm, "radius": 2.5 * mm});
            skCircle(sketch, "E6.0.16.1", {"center": v(157.5, 18.75) * mm, "radius": 2.5 * mm});
            skCircle(sketch, "E6.0.16.2", {"center": v(-112.5, 18.75) * mm, "radius": 2.5 * mm});
            skCircle(sketch, "E6.0.16.3", {"center": v(127.5, 18.75) * mm, "radius": 2.5 * mm});
            skCircle(sketch, "E6.0.16.4", {"center": v(-127.5, 18.75) * mm, "radius": 2.5 * mm});
            skCircle(sketch, "E6.0.16.5", {"center": v(112.5, 18.75) * mm, "radius": 2.5 * mm});
            skCircle(sketch, "E6.0.16.6", {"center": v(-142.5, 18.75) * mm, "radius": 2.5 * mm});
            skCircle(sketch, "E6.0.16.7", {"center": v(97.5, 18.75) * mm, "radius": 2.5 * mm});
            skCircle(sketch, "E6.0.16.8", {"center": v(-157.5, 18.75) * mm, "radius": 2.5 * mm});
            skCircle(sketch, "E6.0.16.9", {"center": v(82.5, 18.75) * mm, "radius": 2.5 * mm});
            skCircle(sketch, "E6.0.16.10", {"center": v(-172.5, 18.75) * mm, "radius": 2.5 * mm});
            skCircle(sketch, "E6.0.16.11", {"center": v(67.5, 18.75) * mm, "radius": 2.5 * mm});
            skCircle(sketch, "E6.0.16.12", {"center": v(-187.5, 18.75) * mm, "radius": 2.5 * mm});
            skCircle(sketch, "E6.0.16.13", {"center": v(52.5, 18.75) * mm, "radius": 2.5 * mm});
            skCircle(sketch, "E6.0.16.14", {"center": v(37.5, 18.75) * mm, "radius": 2.5 * mm});
            skCircle(sketch, "E6.0.16.15", {"center": v(22.5, 18.75) * mm, "radius": 2.5 * mm});
            skCircle(sketch, "E6.0.16.16", {"center": v(7.5, 18.75) * mm, "radius": 2.5 * mm});
            skCircle(sketch, "E6.0.16.17", {"center": v(-7.5, 18.75) * mm, "radius": 2.5 * mm});
            skCircle(sketch, "E6.0.16.18", {"center": v(-22.5, 18.75) * mm, "radius": 2.5 * mm});
            skCircle(sketch, "E6.0.16.19", {"center": v(-37.5, 18.75) * mm, "radius": 2.5 * mm});
            skLineSegment(sketch, "E6.0.16.20", {"start": v(-187.5, 18.75) * mm, "end": v(-172.5, 18.75) * mm, "construction": true});
            skCircle(sketch, "E6.0.16.21", {"center": v(-52.5, 18.75) * mm, "radius": 2.5 * mm});
            skCircle(sketch, "E6.0.16.22", {"center": v(187.5, 18.75) * mm, "radius": 2.5 * mm});
            skCircle(sketch, "E6.0.16.23", {"center": v(-97.5, 18.75) * mm, "radius": 2.5 * mm});
            skCircle(sketch, "E6.0.16.24", {"center": v(142.5, 18.75) * mm, "radius": 2.5 * mm});
            skCircle(sketch, "E6.0.16.25", {"center": v(-67.5, 18.75) * mm, "radius": 2.5 * mm});
            skCircle(sketch, "E6.0.16.26", {"center": v(172.5, 18.75) * mm, "radius": 2.5 * mm});
            skCircle(sketch, "E6.0.17.0", {"center": v(-82.5, 43.75) * mm, "radius": 2.5 * mm});
            skCircle(sketch, "E6.0.17.1", {"center": v(157.5, 43.75) * mm, "radius": 2.5 * mm});
            skCircle(sketch, "E6.0.17.2", {"center": v(-112.5, 43.75) * mm, "radius": 2.5 * mm});
            skCircle(sketch, "E6.0.17.3", {"center": v(127.5, 43.75) * mm, "radius": 2.5 * mm});
            skCircle(sketch, "E6.0.17.4", {"center": v(-127.5, 43.75) * mm, "radius": 2.5 * mm});
            skCircle(sketch, "E6.0.17.5", {"center": v(112.5, 43.75) * mm, "radius": 2.5 * mm});
            skCircle(sketch, "E6.0.17.6", {"center": v(-142.5, 43.75) * mm, "radius": 2.5 * mm});
            skCircle(sketch, "E6.0.17.7", {"center": v(97.5, 43.75) * mm, "radius": 2.5 * mm});
            skCircle(sketch, "E6.0.17.8", {"center": v(-157.5, 43.75) * mm, "radius": 2.5 * mm});
            skCircle(sketch, "E6.0.17.9", {"center": v(82.5, 43.75) * mm, "radius": 2.5 * mm});
            skCircle(sketch, "E6.0.17.10", {"center": v(-172.5, 43.75) * mm, "radius": 2.5 * mm});
            skCircle(sketch, "E6.0.17.11", {"center": v(67.5, 43.75) * mm, "radius": 2.5 * mm});
            skCircle(sketch, "E6.0.17.12", {"center": v(-187.5, 43.75) * mm, "radius": 2.5 * mm});
            skCircle(sketch, "E6.0.17.13", {"center": v(52.5, 43.75) * mm, "radius": 2.5 * mm});
            skCircle(sketch, "E6.0.17.14", {"center": v(37.5, 43.75) * mm, "radius": 2.5 * mm});
            skCircle(sketch, "E6.0.17.15", {"center": v(22.5, 43.75) * mm, "radius": 2.5 * mm});
            skCircle(sketch, "E6.0.17.16", {"center": v(7.5, 43.75) * mm, "radius": 2.5 * mm});
            skCircle(sketch, "E6.0.17.17", {"center": v(-7.5, 43.75) * mm, "radius": 2.5 * mm});
            skCircle(sketch, "E6.0.17.18", {"center": v(-22.5, 43.75) * mm, "radius": 2.5 * mm});
            skCircle(sketch, "E6.0.17.19", {"center": v(-37.5, 43.75) * mm, "radius": 2.5 * mm});
            skLineSegment(sketch, "E6.0.17.20", {"start": v(-187.5, 43.75) * mm, "end": v(-172.5, 43.75) * mm, "construction": true});
            skCircle(sketch, "E6.0.17.21", {"center": v(-52.5, 43.75) * mm, "radius": 2.5 * mm});
            skCircle(sketch, "E6.0.17.22", {"center": v(187.5, 43.75) * mm, "radius": 2.5 * mm});
            skCircle(sketch, "E6.0.17.23", {"center": v(-97.5, 43.75) * mm, "radius": 2.5 * mm});
            skCircle(sketch, "E6.0.17.24", {"center": v(142.5, 43.75) * mm, "radius": 2.5 * mm});
            skCircle(sketch, "E6.0.17.25", {"center": v(-67.5, 43.75) * mm, "radius": 2.5 * mm});
            skCircle(sketch, "E6.0.17.26", {"center": v(172.5, 43.75) * mm, "radius": 2.5 * mm});
            skCircle(sketch, "E6.0.18.0", {"center": v(-82.5, 68.75) * mm, "radius": 2.5 * mm});
            skCircle(sketch, "E6.0.18.1", {"center": v(157.5, 68.75) * mm, "radius": 2.5 * mm});
            skCircle(sketch, "E6.0.18.2", {"center": v(-112.5, 68.75) * mm, "radius": 2.5 * mm});
            skCircle(sketch, "E6.0.18.3", {"center": v(127.5, 68.75) * mm, "radius": 2.5 * mm});
            skCircle(sketch, "E6.0.18.4", {"center": v(-127.5, 68.75) * mm, "radius": 2.5 * mm});
            skCircle(sketch, "E6.0.18.5", {"center": v(112.5, 68.75) * mm, "radius": 2.5 * mm});
            skCircle(sketch, "E6.0.18.6", {"center": v(-142.5, 68.75) * mm, "radius": 2.5 * mm});
            skCircle(sketch, "E6.0.18.7", {"center": v(97.5, 68.75) * mm, "radius": 2.5 * mm});
            skCircle(sketch, "E6.0.18.8", {"center": v(-157.5, 68.75) * mm, "radius": 2.5 * mm});
            skCircle(sketch, "E6.0.18.9", {"center": v(82.5, 68.75) * mm, "radius": 2.5 * mm});
            skCircle(sketch, "E6.0.18.10", {"center": v(-172.5, 68.75) * mm, "radius": 2.5 * mm});
            skCircle(sketch, "E6.0.18.11", {"center": v(67.5, 68.75) * mm, "radius": 2.5 * mm});
            skCircle(sketch, "E6.0.18.12", {"center": v(-187.5, 68.75) * mm, "radius": 2.5 * mm});
            skCircle(sketch, "E6.0.18.13", {"center": v(52.5, 68.75) * mm, "radius": 2.5 * mm});
            skCircle(sketch, "E6.0.18.14", {"center": v(37.5, 68.75) * mm, "radius": 2.5 * mm});
            skCircle(sketch, "E6.0.18.15", {"center": v(22.5, 68.75) * mm, "radius": 2.5 * mm});
            skCircle(sketch, "E6.0.18.16", {"center": v(7.5, 68.75) * mm, "radius": 2.5 * mm});
            skCircle(sketch, "E6.0.18.17", {"center": v(-7.5, 68.75) * mm, "radius": 2.5 * mm});
            skCircle(sketch, "E6.0.18.18", {"center": v(-22.5, 68.75) * mm, "radius": 2.5 * mm});
            skCircle(sketch, "E6.0.18.19", {"center": v(-37.5, 68.75) * mm, "radius": 2.5 * mm});
            skLineSegment(sketch, "E6.0.18.20", {"start": v(-187.5, 68.75) * mm, "end": v(-172.5, 68.75) * mm, "construction": true});
            skCircle(sketch, "E6.0.18.21", {"center": v(-52.5, 68.75) * mm, "radius": 2.5 * mm});
            skCircle(sketch, "E6.0.18.22", {"center": v(187.5, 68.75) * mm, "radius": 2.5 * mm});
            skCircle(sketch, "E6.0.18.23", {"center": v(-97.5, 68.75) * mm, "radius": 2.5 * mm});
            skCircle(sketch, "E6.0.18.24", {"center": v(142.5, 68.75) * mm, "radius": 2.5 * mm});
            skCircle(sketch, "E6.0.18.25", {"center": v(-67.5, 68.75) * mm, "radius": 2.5 * mm});
            skCircle(sketch, "E6.0.18.26", {"center": v(172.5, 68.75) * mm, "radius": 2.5 * mm});
            skCircle(sketch, "E6.0.19.0", {"center": v(-82.5, 93.75) * mm, "radius": 2.5 * mm});
            skCircle(sketch, "E6.0.19.1", {"center": v(157.5, 93.75) * mm, "radius": 2.5 * mm});
            skCircle(sketch, "E6.0.19.2", {"center": v(-112.5, 93.75) * mm, "radius": 2.5 * mm});
            skCircle(sketch, "E6.0.19.3", {"center": v(127.5, 93.75) * mm, "radius": 2.5 * mm});
            skCircle(sketch, "E6.0.19.4", {"center": v(-127.5, 93.75) * mm, "radius": 2.5 * mm});
            skCircle(sketch, "E6.0.19.5", {"center": v(112.5, 93.75) * mm, "radius": 2.5 * mm});
            skCircle(sketch, "E6.0.19.6", {"center": v(-142.5, 93.75) * mm, "radius": 2.5 * mm});
            skCircle(sketch, "E6.0.19.7", {"center": v(97.5, 93.75) * mm, "radius": 2.5 * mm});
            skCircle(sketch, "E6.0.19.8", {"center": v(-157.5, 93.75) * mm, "radius": 2.5 * mm});
            skCircle(sketch, "E6.0.19.9", {"center": v(82.5, 93.75) * mm, "radius": 2.5 * mm});
            skCircle(sketch, "E6.0.19.10", {"center": v(-172.5, 93.75) * mm, "radius": 2.5 * mm});
            skCircle(sketch, "E6.0.19.11", {"center": v(67.5, 93.75) * mm, "radius": 2.5 * mm});
            skCircle(sketch, "E6.0.19.12", {"center": v(-187.5, 93.75) * mm, "radius": 2.5 * mm});
            skCircle(sketch, "E6.0.19.13", {"center": v(52.5, 93.75) * mm, "radius": 2.5 * mm});
            skCircle(sketch, "E6.0.19.14", {"center": v(37.5, 93.75) * mm, "radius": 2.5 * mm});
            skCircle(sketch, "E6.0.19.15", {"center": v(22.5, 93.75) * mm, "radius": 2.5 * mm});
            skCircle(sketch, "E6.0.19.16", {"center": v(7.5, 93.75) * mm, "radius": 2.5 * mm});
            skCircle(sketch, "E6.0.19.17", {"center": v(-7.5, 93.75) * mm, "radius": 2.5 * mm});
            skCircle(sketch, "E6.0.19.18", {"center": v(-22.5, 93.75) * mm, "radius": 2.5 * mm});
            skCircle(sketch, "E6.0.19.19", {"center": v(-37.5, 93.75) * mm, "radius": 2.5 * mm});
            skLineSegment(sketch, "E6.0.19.20", {"start": v(-187.5, 93.75) * mm, "end": v(-172.5, 93.75) * mm, "construction": true});
            skCircle(sketch, "E6.0.19.21", {"center": v(-52.5, 93.75) * mm, "radius": 2.5 * mm});
            skCircle(sketch, "E6.0.19.22", {"center": v(187.5, 93.75) * mm, "radius": 2.5 * mm});
            skCircle(sketch, "E6.0.19.23", {"center": v(-97.5, 93.75) * mm, "radius": 2.5 * mm});
            skCircle(sketch, "E6.0.19.24", {"center": v(142.5, 93.75) * mm, "radius": 2.5 * mm});
            skCircle(sketch, "E6.0.19.25", {"center": v(-67.5, 93.75) * mm, "radius": 2.5 * mm});
            skCircle(sketch, "E6.0.19.26", {"center": v(172.5, 93.75) * mm, "radius": 2.5 * mm});
            skCircle(sketch, "E6.0.20.0", {"center": v(-82.5, 118.75) * mm, "radius": 2.5 * mm});
            skCircle(sketch, "E6.0.20.1", {"center": v(157.5, 118.75) * mm, "radius": 2.5 * mm});
            skCircle(sketch, "E6.0.20.2", {"center": v(-112.5, 118.75) * mm, "radius": 2.5 * mm});
            skCircle(sketch, "E6.0.20.3", {"center": v(127.5, 118.75) * mm, "radius": 2.5 * mm});
            skCircle(sketch, "E6.0.20.4", {"center": v(-127.5, 118.75) * mm, "radius": 2.5 * mm});
            skCircle(sketch, "E6.0.20.5", {"center": v(112.5, 118.75) * mm, "radius": 2.5 * mm});
            skCircle(sketch, "E6.0.20.6", {"center": v(-142.5, 118.75) * mm, "radius": 2.5 * mm});
            skCircle(sketch, "E6.0.20.7", {"center": v(97.5, 118.75) * mm, "radius": 2.5 * mm});
            skCircle(sketch, "E6.0.20.8", {"center": v(-157.5, 118.75) * mm, "radius": 2.5 * mm});
            skCircle(sketch, "E6.0.20.9", {"center": v(82.5, 118.75) * mm, "radius": 2.5 * mm});
            skCircle(sketch, "E6.0.20.10", {"center": v(-172.5, 118.75) * mm, "radius": 2.5 * mm});
            skCircle(sketch, "E6.0.20.11", {"center": v(67.5, 118.75) * mm, "radius": 2.5 * mm});
            skCircle(sketch, "E6.0.20.12", {"center": v(-187.5, 118.75) * mm, "radius": 2.5 * mm});
            skCircle(sketch, "E6.0.20.13", {"center": v(52.5, 118.75) * mm, "radius": 2.5 * mm});
            skCircle(sketch, "E6.0.20.14", {"center": v(37.5, 118.75) * mm, "radius": 2.5 * mm});
            skCircle(sketch, "E6.0.20.15", {"center": v(22.5, 118.75) * mm, "radius": 2.5 * mm});
            skCircle(sketch, "E6.0.20.16", {"center": v(7.5, 118.75) * mm, "radius": 2.5 * mm});
            skCircle(sketch, "E6.0.20.17", {"center": v(-7.5, 118.75) * mm, "radius": 2.5 * mm});
            skCircle(sketch, "E6.0.20.18", {"center": v(-22.5, 118.75) * mm, "radius": 2.5 * mm});
            skCircle(sketch, "E6.0.20.19", {"center": v(-37.5, 118.75) * mm, "radius": 2.5 * mm});
            skLineSegment(sketch, "E6.0.20.20", {"start": v(-187.5, 118.75) * mm, "end": v(-172.5, 118.75) * mm, "construction": true});
            skCircle(sketch, "E6.0.20.21", {"center": v(-52.5, 118.75) * mm, "radius": 2.5 * mm});
            skCircle(sketch, "E6.0.20.22", {"center": v(187.5, 118.75) * mm, "radius": 2.5 * mm});
            skCircle(sketch, "E6.0.20.23", {"center": v(-97.5, 118.75) * mm, "radius": 2.5 * mm});
            skCircle(sketch, "E6.0.20.24", {"center": v(142.5, 118.75) * mm, "radius": 2.5 * mm});
            skCircle(sketch, "E6.0.20.25", {"center": v(-67.5, 118.75) * mm, "radius": 2.5 * mm});
            skCircle(sketch, "E6.0.20.26", {"center": v(172.5, 118.75) * mm, "radius": 2.5 * mm});
            skCircle(sketch, "E6.0.21.0", {"center": v(-82.5, 143.75) * mm, "radius": 2.5 * mm});
            skCircle(sketch, "E6.0.21.1", {"center": v(157.5, 143.75) * mm, "radius": 2.5 * mm});
            skCircle(sketch, "E6.0.21.2", {"center": v(-112.5, 143.75) * mm, "radius": 2.5 * mm});
            skCircle(sketch, "E6.0.21.3", {"center": v(127.5, 143.75) * mm, "radius": 2.5 * mm});
            skCircle(sketch, "E6.0.21.4", {"center": v(-127.5, 143.75) * mm, "radius": 2.5 * mm});
            skCircle(sketch, "E6.0.21.5", {"center": v(112.5, 143.75) * mm, "radius": 2.5 * mm});
            skCircle(sketch, "E6.0.21.6", {"center": v(-142.5, 143.75) * mm, "radius": 2.5 * mm});
            skCircle(sketch, "E6.0.21.7", {"center": v(97.5, 143.75) * mm, "radius": 2.5 * mm});
            skCircle(sketch, "E6.0.21.8", {"center": v(-157.5, 143.75) * mm, "radius": 2.5 * mm});
            skCircle(sketch, "E6.0.21.9", {"center": v(82.5, 143.75) * mm, "radius": 2.5 * mm});
            skCircle(sketch, "E6.0.21.10", {"center": v(-172.5, 143.75) * mm, "radius": 2.5 * mm});
            skCircle(sketch, "E6.0.21.11", {"center": v(67.5, 143.75) * mm, "radius": 2.5 * mm});
            skCircle(sketch, "E6.0.21.12", {"center": v(-187.5, 143.75) * mm, "radius": 2.5 * mm});
            skCircle(sketch, "E6.0.21.13", {"center": v(52.5, 143.75) * mm, "radius": 2.5 * mm});
            skCircle(sketch, "E6.0.21.14", {"center": v(37.5, 143.75) * mm, "radius": 2.5 * mm});
            skCircle(sketch, "E6.0.21.15", {"center": v(22.5, 143.75) * mm, "radius": 2.5 * mm});
            skCircle(sketch, "E6.0.21.16", {"center": v(7.5, 143.75) * mm, "radius": 2.5 * mm});
            skCircle(sketch, "E6.0.21.17", {"center": v(-7.5, 143.75) * mm, "radius": 2.5 * mm});
            skCircle(sketch, "E6.0.21.18", {"center": v(-22.5, 143.75) * mm, "radius": 2.5 * mm});
            skCircle(sketch, "E6.0.21.19", {"center": v(-37.5, 143.75) * mm, "radius": 2.5 * mm});
            skLineSegment(sketch, "E6.0.21.20", {"start": v(-187.5, 143.75) * mm, "end": v(-172.5, 143.75) * mm, "construction": true});
            skCircle(sketch, "E6.0.21.21", {"center": v(-52.5, 143.75) * mm, "radius": 2.5 * mm});
            skCircle(sketch, "E6.0.21.22", {"center": v(187.5, 143.75) * mm, "radius": 2.5 * mm});
            skCircle(sketch, "E6.0.21.23", {"center": v(-97.5, 143.75) * mm, "radius": 2.5 * mm});
            skCircle(sketch, "E6.0.21.24", {"center": v(142.5, 143.75) * mm, "radius": 2.5 * mm});
            skCircle(sketch, "E6.0.21.25", {"center": v(-67.5, 143.75) * mm, "radius": 2.5 * mm});
            skCircle(sketch, "E6.0.21.26", {"center": v(172.5, 143.75) * mm, "radius": 2.5 * mm});
            skCircle(sketch, "E6.0.22.0", {"center": v(-82.5, 168.75) * mm, "radius": 2.5 * mm});
            skCircle(sketch, "E6.0.22.1", {"center": v(157.5, 168.75) * mm, "radius": 2.5 * mm});
            skCircle(sketch, "E6.0.22.2", {"center": v(-112.5, 168.75) * mm, "radius": 2.5 * mm});
            skCircle(sketch, "E6.0.22.3", {"center": v(127.5, 168.75) * mm, "radius": 2.5 * mm});
            skCircle(sketch, "E6.0.22.4", {"center": v(-127.5, 168.75) * mm, "radius": 2.5 * mm});
            skCircle(sketch, "E6.0.22.5", {"center": v(112.5, 168.75) * mm, "radius": 2.5 * mm});
            skCircle(sketch, "E6.0.22.6", {"center": v(-142.5, 168.75) * mm, "radius": 2.5 * mm});
            skCircle(sketch, "E6.0.22.7", {"center": v(97.5, 168.75) * mm, "radius": 2.5 * mm});
            skCircle(sketch, "E6.0.22.8", {"center": v(-157.5, 168.75) * mm, "radius": 2.5 * mm});
            skCircle(sketch, "E6.0.22.9", {"center": v(82.5, 168.75) * mm, "radius": 2.5 * mm});
            skCircle(sketch, "E6.0.22.10", {"center": v(-172.5, 168.75) * mm, "radius": 2.5 * mm});
            skCircle(sketch, "E6.0.22.11", {"center": v(67.5, 168.75) * mm, "radius": 2.5 * mm});
            skCircle(sketch, "E6.0.22.12", {"center": v(-187.5, 168.75) * mm, "radius": 2.5 * mm});
            skCircle(sketch, "E6.0.22.13", {"center": v(52.5, 168.75) * mm, "radius": 2.5 * mm});
            skCircle(sketch, "E6.0.22.14", {"center": v(37.5, 168.75) * mm, "radius": 2.5 * mm});
            skCircle(sketch, "E6.0.22.15", {"center": v(22.5, 168.75) * mm, "radius": 2.5 * mm});
            skCircle(sketch, "E6.0.22.16", {"center": v(7.5, 168.75) * mm, "radius": 2.5 * mm});
            skCircle(sketch, "E6.0.22.17", {"center": v(-7.5, 168.75) * mm, "radius": 2.5 * mm});
            skCircle(sketch, "E6.0.22.18", {"center": v(-22.5, 168.75) * mm, "radius": 2.5 * mm});
            skCircle(sketch, "E6.0.22.19", {"center": v(-37.5, 168.75) * mm, "radius": 2.5 * mm});
            skLineSegment(sketch, "E6.0.22.20", {"start": v(-187.5, 168.75) * mm, "end": v(-172.5, 168.75) * mm, "construction": true});
            skCircle(sketch, "E6.0.22.21", {"center": v(-52.5, 168.75) * mm, "radius": 2.5 * mm});
            skCircle(sketch, "E6.0.22.22", {"center": v(187.5, 168.75) * mm, "radius": 2.5 * mm});
            skCircle(sketch, "E6.0.22.23", {"center": v(-97.5, 168.75) * mm, "radius": 2.5 * mm});
            skCircle(sketch, "E6.0.22.24", {"center": v(142.5, 168.75) * mm, "radius": 2.5 * mm});
            skCircle(sketch, "E6.0.22.25", {"center": v(-67.5, 168.75) * mm, "radius": 2.5 * mm});
            skCircle(sketch, "E6.0.22.26", {"center": v(172.5, 168.75) * mm, "radius": 2.5 * mm});
            skCircle(sketch, "E6.0.23.0", {"center": v(-82.5, 193.75) * mm, "radius": 2.5 * mm});
            skCircle(sketch, "E6.0.23.1", {"center": v(157.5, 193.75) * mm, "radius": 2.5 * mm});
            skCircle(sketch, "E6.0.23.2", {"center": v(-112.5, 193.75) * mm, "radius": 2.5 * mm});
            skCircle(sketch, "E6.0.23.3", {"center": v(127.5, 193.75) * mm, "radius": 2.5 * mm});
            skCircle(sketch, "E6.0.23.4", {"center": v(-127.5, 193.75) * mm, "radius": 2.5 * mm});
            skCircle(sketch, "E6.0.23.5", {"center": v(112.5, 193.75) * mm, "radius": 2.5 * mm});
            skCircle(sketch, "E6.0.23.6", {"center": v(-142.5, 193.75) * mm, "radius": 2.5 * mm});
            skCircle(sketch, "E6.0.23.7", {"center": v(97.5, 193.75) * mm, "radius": 2.5 * mm});
            skCircle(sketch, "E6.0.23.8", {"center": v(-157.5, 193.75) * mm, "radius": 2.5 * mm});
            skCircle(sketch, "E6.0.23.9", {"center": v(82.5, 193.75) * mm, "radius": 2.5 * mm});
            skCircle(sketch, "E6.0.23.10", {"center": v(-172.5, 193.75) * mm, "radius": 2.5 * mm});
            skCircle(sketch, "E6.0.23.11", {"center": v(67.5, 193.75) * mm, "radius": 2.5 * mm});
            skCircle(sketch, "E6.0.23.12", {"center": v(-187.5, 193.75) * mm, "radius": 2.5 * mm});
            skCircle(sketch, "E6.0.23.13", {"center": v(52.5, 193.75) * mm, "radius": 2.5 * mm});
            skCircle(sketch, "E6.0.23.14", {"center": v(37.5, 193.75) * mm, "radius": 2.5 * mm});
            skCircle(sketch, "E6.0.23.15", {"center": v(22.5, 193.75) * mm, "radius": 2.5 * mm});
            skCircle(sketch, "E6.0.23.16", {"center": v(7.5, 193.75) * mm, "radius": 2.5 * mm});
            skCircle(sketch, "E6.0.23.17", {"center": v(-7.5, 193.75) * mm, "radius": 2.5 * mm});
            skCircle(sketch, "E6.0.23.18", {"center": v(-22.5, 193.75) * mm, "radius": 2.5 * mm});
            skCircle(sketch, "E6.0.23.19", {"center": v(-37.5, 193.75) * mm, "radius": 2.5 * mm});
            skLineSegment(sketch, "E6.0.23.20", {"start": v(-187.5, 193.75) * mm, "end": v(-172.5, 193.75) * mm, "construction": true});
            skCircle(sketch, "E6.0.23.21", {"center": v(-52.5, 193.75) * mm, "radius": 2.5 * mm});
            skCircle(sketch, "E6.0.23.22", {"center": v(187.5, 193.75) * mm, "radius": 2.5 * mm});
            skCircle(sketch, "E6.0.23.23", {"center": v(-97.5, 193.75) * mm, "radius": 2.5 * mm});
            skCircle(sketch, "E6.0.23.24", {"center": v(142.5, 193.75) * mm, "radius": 2.5 * mm});
            skCircle(sketch, "E6.0.23.25", {"center": v(-67.5, 193.75) * mm, "radius": 2.5 * mm});
            skCircle(sketch, "E6.0.23.26", {"center": v(172.5, 193.75) * mm, "radius": 2.5 * mm});
            skCircle(sketch, "E6.0.24.0", {"center": v(-82.5, 218.75) * mm, "radius": 2.5 * mm});
            skCircle(sketch, "E6.0.24.1", {"center": v(157.5, 218.75) * mm, "radius": 2.5 * mm});
            skCircle(sketch, "E6.0.24.2", {"center": v(-112.5, 218.75) * mm, "radius": 2.5 * mm});
            skCircle(sketch, "E6.0.24.3", {"center": v(127.5, 218.75) * mm, "radius": 2.5 * mm});
            skCircle(sketch, "E6.0.24.4", {"center": v(-127.5, 218.75) * mm, "radius": 2.5 * mm});
            skCircle(sketch, "E6.0.24.5", {"center": v(112.5, 218.75) * mm, "radius": 2.5 * mm});
            skCircle(sketch, "E6.0.24.6", {"center": v(-142.5, 218.75) * mm, "radius": 2.5 * mm});
            skCircle(sketch, "E6.0.24.7", {"center": v(97.5, 218.75) * mm, "radius": 2.5 * mm});
            skCircle(sketch, "E6.0.24.8", {"center": v(-157.5, 218.75) * mm, "radius": 2.5 * mm});
            skCircle(sketch, "E6.0.24.9", {"center": v(82.5, 218.75) * mm, "radius": 2.5 * mm});
            skCircle(sketch, "E6.0.24.10", {"center": v(-172.5, 218.75) * mm, "radius": 2.5 * mm});
            skCircle(sketch, "E6.0.24.11", {"center": v(67.5, 218.75) * mm, "radius": 2.5 * mm});
            skCircle(sketch, "E6.0.24.12", {"center": v(-187.5, 218.75) * mm, "radius": 2.5 * mm});
            skCircle(sketch, "E6.0.24.13", {"center": v(52.5, 218.75) * mm, "radius": 2.5 * mm});
            skCircle(sketch, "E6.0.24.14", {"center": v(37.5, 218.75) * mm, "radius": 2.5 * mm});
            skCircle(sketch, "E6.0.24.15", {"center": v(22.5, 218.75) * mm, "radius": 2.5 * mm});
            skCircle(sketch, "E6.0.24.16", {"center": v(7.5, 218.75) * mm, "radius": 2.5 * mm});
            skCircle(sketch, "E6.0.24.17", {"center": v(-7.5, 218.75) * mm, "radius": 2.5 * mm});
            skCircle(sketch, "E6.0.24.18", {"center": v(-22.5, 218.75) * mm, "radius": 2.5 * mm});
            skCircle(sketch, "E6.0.24.19", {"center": v(-37.5, 218.75) * mm, "radius": 2.5 * mm});
            skLineSegment(sketch, "E6.0.24.20", {"start": v(-187.5, 218.75) * mm, "end": v(-172.5, 218.75) * mm, "construction": true});
            skCircle(sketch, "E6.0.24.21", {"center": v(-52.5, 218.75) * mm, "radius": 2.5 * mm});
            skCircle(sketch, "E6.0.24.22", {"center": v(187.5, 218.75) * mm, "radius": 2.5 * mm});
            skCircle(sketch, "E6.0.24.23", {"center": v(-97.5, 218.75) * mm, "radius": 2.5 * mm});
            skCircle(sketch, "E6.0.24.24", {"center": v(142.5, 218.75) * mm, "radius": 2.5 * mm});
            skCircle(sketch, "E6.0.24.25", {"center": v(-67.5, 218.75) * mm, "radius": 2.5 * mm});
            skCircle(sketch, "E6.0.24.26", {"center": v(172.5, 218.75) * mm, "radius": 2.5 * mm});
            skCircle(sketch, "E6.0.25.0", {"center": v(-82.5, 243.75) * mm, "radius": 2.5 * mm});
            skCircle(sketch, "E6.0.25.1", {"center": v(157.5, 243.75) * mm, "radius": 2.5 * mm});
            skCircle(sketch, "E6.0.25.2", {"center": v(-112.5, 243.75) * mm, "radius": 2.5 * mm});
            skCircle(sketch, "E6.0.25.3", {"center": v(127.5, 243.75) * mm, "radius": 2.5 * mm});
            skCircle(sketch, "E6.0.25.4", {"center": v(-127.5, 243.75) * mm, "radius": 2.5 * mm});
            skCircle(sketch, "E6.0.25.5", {"center": v(112.5, 243.75) * mm, "radius": 2.5 * mm});
            skCircle(sketch, "E6.0.25.6", {"center": v(-142.5, 243.75) * mm, "radius": 2.5 * mm});
            skCircle(sketch, "E6.0.25.7", {"center": v(97.5, 243.75) * mm, "radius": 2.5 * mm});
            skCircle(sketch, "E6.0.25.8", {"center": v(-157.5, 243.75) * mm, "radius": 2.5 * mm});
            skCircle(sketch, "E6.0.25.9", {"center": v(82.5, 243.75) * mm, "radius": 2.5 * mm});
            skCircle(sketch, "E6.0.25.10", {"center": v(-172.5, 243.75) * mm, "radius": 2.5 * mm});
            skCircle(sketch, "E6.0.25.11", {"center": v(67.5, 243.75) * mm, "radius": 2.5 * mm});
            skCircle(sketch, "E6.0.25.12", {"center": v(-187.5, 243.75) * mm, "radius": 2.5 * mm});
            skCircle(sketch, "E6.0.25.13", {"center": v(52.5, 243.75) * mm, "radius": 2.5 * mm});
            skCircle(sketch, "E6.0.25.14", {"center": v(37.5, 243.75) * mm, "radius": 2.5 * mm});
            skCircle(sketch, "E6.0.25.15", {"center": v(22.5, 243.75) * mm, "radius": 2.5 * mm});
            skCircle(sketch, "E6.0.25.16", {"center": v(7.5, 243.75) * mm, "radius": 2.5 * mm});
            skCircle(sketch, "E6.0.25.17", {"center": v(-7.5, 243.75) * mm, "radius": 2.5 * mm});
            skCircle(sketch, "E6.0.25.18", {"center": v(-22.5, 243.75) * mm, "radius": 2.5 * mm});
            skCircle(sketch, "E6.0.25.19", {"center": v(-37.5, 243.75) * mm, "radius": 2.5 * mm});
            skLineSegment(sketch, "E6.0.25.20", {"start": v(-187.5, 243.75) * mm, "end": v(-172.5, 243.75) * mm, "construction": true});
            skCircle(sketch, "E6.0.25.21", {"center": v(-52.5, 243.75) * mm, "radius": 2.5 * mm});
            skCircle(sketch, "E6.0.25.22", {"center": v(187.5, 243.75) * mm, "radius": 2.5 * mm});
            skCircle(sketch, "E6.0.25.23", {"center": v(-97.5, 243.75) * mm, "radius": 2.5 * mm});
            skCircle(sketch, "E6.0.25.24", {"center": v(142.5, 243.75) * mm, "radius": 2.5 * mm});
            skCircle(sketch, "E6.0.25.25", {"center": v(-67.5, 243.75) * mm, "radius": 2.5 * mm});
            skCircle(sketch, "E6.0.25.26", {"center": v(172.5, 243.75) * mm, "radius": 2.5 * mm});
            skCircle(sketch, "E6.0.26.0", {"center": v(-82.5, 268.75) * mm, "radius": 2.5 * mm});
            skCircle(sketch, "E6.0.26.1", {"center": v(157.5, 268.75) * mm, "radius": 2.5 * mm});
            skCircle(sketch, "E6.0.26.2", {"center": v(-112.5, 268.75) * mm, "radius": 2.5 * mm});
            skCircle(sketch, "E6.0.26.3", {"center": v(127.5, 268.75) * mm, "radius": 2.5 * mm});
            skCircle(sketch, "E6.0.26.4", {"center": v(-127.5, 268.75) * mm, "radius": 2.5 * mm});
            skCircle(sketch, "E6.0.26.5", {"center": v(112.5, 268.75) * mm, "radius": 2.5 * mm});
            skCircle(sketch, "E6.0.26.6", {"center": v(-142.5, 268.75) * mm, "radius": 2.5 * mm});
            skCircle(sketch, "E6.0.26.7", {"center": v(97.5, 268.75) * mm, "radius": 2.5 * mm});
            skCircle(sketch, "E6.0.26.8", {"center": v(-157.5, 268.75) * mm, "radius": 2.5 * mm});
            skCircle(sketch, "E6.0.26.9", {"center": v(82.5, 268.75) * mm, "radius": 2.5 * mm});
            skCircle(sketch, "E6.0.26.10", {"center": v(-172.5, 268.75) * mm, "radius": 2.5 * mm});
            skCircle(sketch, "E6.0.26.11", {"center": v(67.5, 268.75) * mm, "radius": 2.5 * mm});
            skCircle(sketch, "E6.0.26.12", {"center": v(-187.5, 268.75) * mm, "radius": 2.5 * mm});
            skCircle(sketch, "E6.0.26.13", {"center": v(52.5, 268.75) * mm, "radius": 2.5 * mm});
            skCircle(sketch, "E6.0.26.14", {"center": v(37.5, 268.75) * mm, "radius": 2.5 * mm});
            skCircle(sketch, "E6.0.26.15", {"center": v(22.5, 268.75) * mm, "radius": 2.5 * mm});
            skCircle(sketch, "E6.0.26.16", {"center": v(7.5, 268.75) * mm, "radius": 2.5 * mm});
            skCircle(sketch, "E6.0.26.17", {"center": v(-7.5, 268.75) * mm, "radius": 2.5 * mm});
            skCircle(sketch, "E6.0.26.18", {"center": v(-22.5, 268.75) * mm, "radius": 2.5 * mm});
            skCircle(sketch, "E6.0.26.19", {"center": v(-37.5, 268.75) * mm, "radius": 2.5 * mm});
            skLineSegment(sketch, "E6.0.26.20", {"start": v(-187.5, 268.75) * mm, "end": v(-172.5, 268.75) * mm, "construction": true});
            skCircle(sketch, "E6.0.26.21", {"center": v(-52.5, 268.75) * mm, "radius": 2.5 * mm});
            skCircle(sketch, "E6.0.26.22", {"center": v(187.5, 268.75) * mm, "radius": 2.5 * mm});
            skCircle(sketch, "E6.0.26.23", {"center": v(-97.5, 268.75) * mm, "radius": 2.5 * mm});
            skCircle(sketch, "E6.0.26.24", {"center": v(142.5, 268.75) * mm, "radius": 2.5 * mm});
            skCircle(sketch, "E6.0.26.25", {"center": v(-67.5, 268.75) * mm, "radius": 2.5 * mm});
            skCircle(sketch, "E6.0.26.26", {"center": v(172.5, 268.75) * mm, "radius": 2.5 * mm});
            skCircle(sketch, "E6.0.27.0", {"center": v(-82.5, 293.75) * mm, "radius": 2.5 * mm});
            skCircle(sketch, "E6.0.27.1", {"center": v(157.5, 293.75) * mm, "radius": 2.5 * mm});
            skCircle(sketch, "E6.0.27.2", {"center": v(-112.5, 293.75) * mm, "radius": 2.5 * mm});
            skCircle(sketch, "E6.0.27.3", {"center": v(127.5, 293.75) * mm, "radius": 2.5 * mm});
            skCircle(sketch, "E6.0.27.4", {"center": v(-127.5, 293.75) * mm, "radius": 2.5 * mm});
            skCircle(sketch, "E6.0.27.5", {"center": v(112.5, 293.75) * mm, "radius": 2.5 * mm});
            skCircle(sketch, "E6.0.27.6", {"center": v(-142.5, 293.75) * mm, "radius": 2.5 * mm});
            skCircle(sketch, "E6.0.27.7", {"center": v(97.5, 293.75) * mm, "radius": 2.5 * mm});
            skCircle(sketch, "E6.0.27.8", {"center": v(-157.5, 293.75) * mm, "radius": 2.5 * mm});
            skCircle(sketch, "E6.0.27.9", {"center": v(82.5, 293.75) * mm, "radius": 2.5 * mm});
            skCircle(sketch, "E6.0.27.10", {"center": v(-172.5, 293.75) * mm, "radius": 2.5 * mm});
            skCircle(sketch, "E6.0.27.11", {"center": v(67.5, 293.75) * mm, "radius": 2.5 * mm});
            skCircle(sketch, "E6.0.27.12", {"center": v(-187.5, 293.75) * mm, "radius": 2.5 * mm});
            skCircle(sketch, "E6.0.27.13", {"center": v(52.5, 293.75) * mm, "radius": 2.5 * mm});
            skCircle(sketch, "E6.0.27.14", {"center": v(37.5, 293.75) * mm, "radius": 2.5 * mm});
            skCircle(sketch, "E6.0.27.15", {"center": v(22.5, 293.75) * mm, "radius": 2.5 * mm});
            skCircle(sketch, "E6.0.27.16", {"center": v(7.5, 293.75) * mm, "radius": 2.5 * mm});
            skCircle(sketch, "E6.0.27.17", {"center": v(-7.5, 293.75) * mm, "radius": 2.5 * mm});
            skCircle(sketch, "E6.0.27.18", {"center": v(-22.5, 293.75) * mm, "radius": 2.5 * mm});
            skCircle(sketch, "E6.0.27.19", {"center": v(-37.5, 293.75) * mm, "radius": 2.5 * mm});
            skLineSegment(sketch, "E6.0.27.20", {"start": v(-187.5, 293.75) * mm, "end": v(-172.5, 293.75) * mm, "construction": true});
            skCircle(sketch, "E6.0.27.21", {"center": v(-52.5, 293.75) * mm, "radius": 2.5 * mm});
            skCircle(sketch, "E6.0.27.22", {"center": v(187.5, 293.75) * mm, "radius": 2.5 * mm});
            skCircle(sketch, "E6.0.27.23", {"center": v(-97.5, 293.75) * mm, "radius": 2.5 * mm});
            skCircle(sketch, "E6.0.27.24", {"center": v(142.5, 293.75) * mm, "radius": 2.5 * mm});
            skCircle(sketch, "E6.0.27.25", {"center": v(-67.5, 293.75) * mm, "radius": 2.5 * mm});
            skCircle(sketch, "E6.0.27.26", {"center": v(172.5, 293.75) * mm, "radius": 2.5 * mm});
            skCircle(sketch, "E6.0.28.0", {"center": v(-82.5, 318.75) * mm, "radius": 2.5 * mm});
            skCircle(sketch, "E6.0.28.1", {"center": v(157.5, 318.75) * mm, "radius": 2.5 * mm});
            skCircle(sketch, "E6.0.28.2", {"center": v(-112.5, 318.75) * mm, "radius": 2.5 * mm});
            skCircle(sketch, "E6.0.28.3", {"center": v(127.5, 318.75) * mm, "radius": 2.5 * mm});
            skCircle(sketch, "E6.0.28.4", {"center": v(-127.5, 318.75) * mm, "radius": 2.5 * mm});
            skCircle(sketch, "E6.0.28.5", {"center": v(112.5, 318.75) * mm, "radius": 2.5 * mm});
            skCircle(sketch, "E6.0.28.6", {"center": v(-142.5, 318.75) * mm, "radius": 2.5 * mm});
            skCircle(sketch, "E6.0.28.7", {"center": v(97.5, 318.75) * mm, "radius": 2.5 * mm});
            skCircle(sketch, "E6.0.28.8", {"center": v(-157.5, 318.75) * mm, "radius": 2.5 * mm});
            skCircle(sketch, "E6.0.28.9", {"center": v(82.5, 318.75) * mm, "radius": 2.5 * mm});
            skCircle(sketch, "E6.0.28.10", {"center": v(-172.5, 318.75) * mm, "radius": 2.5 * mm});
            skCircle(sketch, "E6.0.28.11", {"center": v(67.5, 318.75) * mm, "radius": 2.5 * mm});
            skCircle(sketch, "E6.0.28.12", {"center": v(-187.5, 318.75) * mm, "radius": 2.5 * mm});
            skCircle(sketch, "E6.0.28.13", {"center": v(52.5, 318.75) * mm, "radius": 2.5 * mm});
            skCircle(sketch, "E6.0.28.14", {"center": v(37.5, 318.75) * mm, "radius": 2.5 * mm});
            skCircle(sketch, "E6.0.28.15", {"center": v(22.5, 318.75) * mm, "radius": 2.5 * mm});
            skCircle(sketch, "E6.0.28.16", {"center": v(7.5, 318.75) * mm, "radius": 2.5 * mm});
            skCircle(sketch, "E6.0.28.17", {"center": v(-7.5, 318.75) * mm, "radius": 2.5 * mm});
            skCircle(sketch, "E6.0.28.18", {"center": v(-22.5, 318.75) * mm, "radius": 2.5 * mm});
            skCircle(sketch, "E6.0.28.19", {"center": v(-37.5, 318.75) * mm, "radius": 2.5 * mm});
            skLineSegment(sketch, "E6.0.28.20", {"start": v(-187.5, 318.75) * mm, "end": v(-172.5, 318.75) * mm, "construction": true});
            skCircle(sketch, "E6.0.28.21", {"center": v(-52.5, 318.75) * mm, "radius": 2.5 * mm});
            skCircle(sketch, "E6.0.28.22", {"center": v(187.5, 318.75) * mm, "radius": 2.5 * mm});
            skCircle(sketch, "E6.0.28.23", {"center": v(-97.5, 318.75) * mm, "radius": 2.5 * mm});
            skCircle(sketch, "E6.0.28.24", {"center": v(142.5, 318.75) * mm, "radius": 2.5 * mm});
            skCircle(sketch, "E6.0.28.25", {"center": v(-67.5, 318.75) * mm, "radius": 2.5 * mm});
            skCircle(sketch, "E6.0.28.26", {"center": v(172.5, 318.75) * mm, "radius": 2.5 * mm});
            skCircle(sketch, "E6.0.29.0", {"center": v(-82.5, 343.75) * mm, "radius": 2.5 * mm});
            skCircle(sketch, "E6.0.29.1", {"center": v(157.5, 343.75) * mm, "radius": 2.5 * mm});
            skCircle(sketch, "E6.0.29.2", {"center": v(-112.5, 343.75) * mm, "radius": 2.5 * mm});
            skCircle(sketch, "E6.0.29.3", {"center": v(127.5, 343.75) * mm, "radius": 2.5 * mm});
            skCircle(sketch, "E6.0.29.4", {"center": v(-127.5, 343.75) * mm, "radius": 2.5 * mm});
            skCircle(sketch, "E6.0.29.5", {"center": v(112.5, 343.75) * mm, "radius": 2.5 * mm});
            skCircle(sketch, "E6.0.29.6", {"center": v(-142.5, 343.75) * mm, "radius": 2.5 * mm});
            skCircle(sketch, "E6.0.29.7", {"center": v(97.5, 343.75) * mm, "radius": 2.5 * mm});
            skCircle(sketch, "E6.0.29.8", {"center": v(-157.5, 343.75) * mm, "radius": 2.5 * mm});
            skCircle(sketch, "E6.0.29.9", {"center": v(82.5, 343.75) * mm, "radius": 2.5 * mm});
            skCircle(sketch, "E6.0.29.10", {"center": v(-172.5, 343.75) * mm, "radius": 2.5 * mm});
            skCircle(sketch, "E6.0.29.11", {"center": v(67.5, 343.75) * mm, "radius": 2.5 * mm});
            skCircle(sketch, "E6.0.29.12", {"center": v(-187.5, 343.75) * mm, "radius": 2.5 * mm});
            skCircle(sketch, "E6.0.29.13", {"center": v(52.5, 343.75) * mm, "radius": 2.5 * mm});
            skCircle(sketch, "E6.0.29.14", {"center": v(37.5, 343.75) * mm, "radius": 2.5 * mm});
            skCircle(sketch, "E6.0.29.15", {"center": v(22.5, 343.75) * mm, "radius": 2.5 * mm});
            skCircle(sketch, "E6.0.29.16", {"center": v(7.5, 343.75) * mm, "radius": 2.5 * mm});
            skCircle(sketch, "E6.0.29.17", {"center": v(-7.5, 343.75) * mm, "radius": 2.5 * mm});
            skCircle(sketch, "E6.0.29.18", {"center": v(-22.5, 343.75) * mm, "radius": 2.5 * mm});
            skCircle(sketch, "E6.0.29.19", {"center": v(-37.5, 343.75) * mm, "radius": 2.5 * mm});
            skLineSegment(sketch, "E6.0.29.20", {"start": v(-187.5, 343.75) * mm, "end": v(-172.5, 343.75) * mm, "construction": true});
            skCircle(sketch, "E6.0.29.21", {"center": v(-52.5, 343.75) * mm, "radius": 2.5 * mm});
            skCircle(sketch, "E6.0.29.22", {"center": v(187.5, 343.75) * mm, "radius": 2.5 * mm});
            skCircle(sketch, "E6.0.29.23", {"center": v(-97.5, 343.75) * mm, "radius": 2.5 * mm});
            skCircle(sketch, "E6.0.29.24", {"center": v(142.5, 343.75) * mm, "radius": 2.5 * mm});
            skCircle(sketch, "E6.0.29.25", {"center": v(-67.5, 343.75) * mm, "radius": 2.5 * mm});
            skCircle(sketch, "E6.0.29.26", {"center": v(172.5, 343.75) * mm, "radius": 2.5 * mm});
            skCircle(sketch, "E6.0.30.0", {"center": v(-82.5, 368.75) * mm, "radius": 2.5 * mm});
            skCircle(sketch, "E6.0.30.1", {"center": v(157.5, 368.75) * mm, "radius": 2.5 * mm});
            skCircle(sketch, "E6.0.30.2", {"center": v(-112.5, 368.75) * mm, "radius": 2.5 * mm});
            skCircle(sketch, "E6.0.30.3", {"center": v(127.5, 368.75) * mm, "radius": 2.5 * mm});
            skCircle(sketch, "E6.0.30.4", {"center": v(-127.5, 368.75) * mm, "radius": 2.5 * mm});
            skCircle(sketch, "E6.0.30.5", {"center": v(112.5, 368.75) * mm, "radius": 2.5 * mm});
            skCircle(sketch, "E6.0.30.6", {"center": v(-142.5, 368.75) * mm, "radius": 2.5 * mm});
            skCircle(sketch, "E6.0.30.7", {"center": v(97.5, 368.75) * mm, "radius": 2.5 * mm});
            skCircle(sketch, "E6.0.30.8", {"center": v(-157.5, 368.75) * mm, "radius": 2.5 * mm});
            skCircle(sketch, "E6.0.30.9", {"center": v(82.5, 368.75) * mm, "radius": 2.5 * mm});
            skCircle(sketch, "E6.0.30.10", {"center": v(-172.5, 368.75) * mm, "radius": 2.5 * mm});
            skCircle(sketch, "E6.0.30.11", {"center": v(67.5, 368.75) * mm, "radius": 2.5 * mm});
            skCircle(sketch, "E6.0.30.12", {"center": v(-187.5, 368.75) * mm, "radius": 2.5 * mm});
            skCircle(sketch, "E6.0.30.13", {"center": v(52.5, 368.75) * mm, "radius": 2.5 * mm});
            skCircle(sketch, "E6.0.30.14", {"center": v(37.5, 368.75) * mm, "radius": 2.5 * mm});
            skCircle(sketch, "E6.0.30.15", {"center": v(22.5, 368.75) * mm, "radius": 2.5 * mm});
            skCircle(sketch, "E6.0.30.16", {"center": v(7.5, 368.75) * mm, "radius": 2.5 * mm});
            skCircle(sketch, "E6.0.30.17", {"center": v(-7.5, 368.75) * mm, "radius": 2.5 * mm});
            skCircle(sketch, "E6.0.30.18", {"center": v(-22.5, 368.75) * mm, "radius": 2.5 * mm});
            skCircle(sketch, "E6.0.30.19", {"center": v(-37.5, 368.75) * mm, "radius": 2.5 * mm});
            skLineSegment(sketch, "E6.0.30.20", {"start": v(-187.5, 368.75) * mm, "end": v(-172.5, 368.75) * mm, "construction": true});
            skCircle(sketch, "E6.0.30.21", {"center": v(-52.5, 368.75) * mm, "radius": 2.5 * mm});
            skCircle(sketch, "E6.0.30.22", {"center": v(187.5, 368.75) * mm, "radius": 2.5 * mm});
            skCircle(sketch, "E6.0.30.23", {"center": v(-97.5, 368.75) * mm, "radius": 2.5 * mm});
            skCircle(sketch, "E6.0.30.24", {"center": v(142.5, 368.75) * mm, "radius": 2.5 * mm});
            skCircle(sketch, "E6.0.30.25", {"center": v(-67.5, 368.75) * mm, "radius": 2.5 * mm});
            skCircle(sketch, "E6.0.30.26", {"center": v(172.5, 368.75) * mm, "radius": 2.5 * mm});
            skCircle(sketch, "E6.0.31.0", {"center": v(-82.5, 393.75) * mm, "radius": 2.5 * mm});
            skCircle(sketch, "E6.0.31.1", {"center": v(157.5, 393.75) * mm, "radius": 2.5 * mm});
            skCircle(sketch, "E6.0.31.2", {"center": v(-112.5, 393.75) * mm, "radius": 2.5 * mm});
            skCircle(sketch, "E6.0.31.3", {"center": v(127.5, 393.75) * mm, "radius": 2.5 * mm});
            skCircle(sketch, "E6.0.31.4", {"center": v(-127.5, 393.75) * mm, "radius": 2.5 * mm});
            skCircle(sketch, "E6.0.31.5", {"center": v(112.5, 393.75) * mm, "radius": 2.5 * mm});
            skCircle(sketch, "E6.0.31.6", {"center": v(-142.5, 393.75) * mm, "radius": 2.5 * mm});
            skCircle(sketch, "E6.0.31.7", {"center": v(97.5, 393.75) * mm, "radius": 2.5 * mm});
            skCircle(sketch, "E6.0.31.8", {"center": v(-157.5, 393.75) * mm, "radius": 2.5 * mm});
            skCircle(sketch, "E6.0.31.9", {"center": v(82.5, 393.75) * mm, "radius": 2.5 * mm});
            skCircle(sketch, "E6.0.31.10", {"center": v(-172.5, 393.75) * mm, "radius": 2.5 * mm});
            skCircle(sketch, "E6.0.31.11", {"center": v(67.5, 393.75) * mm, "radius": 2.5 * mm});
            skCircle(sketch, "E6.0.31.12", {"center": v(-187.5, 393.75) * mm, "radius": 2.5 * mm});
            skCircle(sketch, "E6.0.31.13", {"center": v(52.5, 393.75) * mm, "radius": 2.5 * mm});
            skCircle(sketch, "E6.0.31.14", {"center": v(37.5, 393.75) * mm, "radius": 2.5 * mm});
            skCircle(sketch, "E6.0.31.15", {"center": v(22.5, 393.75) * mm, "radius": 2.5 * mm});
            skCircle(sketch, "E6.0.31.16", {"center": v(7.5, 393.75) * mm, "radius": 2.5 * mm});
            skCircle(sketch, "E6.0.31.17", {"center": v(-7.5, 393.75) * mm, "radius": 2.5 * mm});
            skCircle(sketch, "E6.0.31.18", {"center": v(-22.5, 393.75) * mm, "radius": 2.5 * mm});
            skCircle(sketch, "E6.0.31.19", {"center": v(-37.5, 393.75) * mm, "radius": 2.5 * mm});
            skLineSegment(sketch, "E6.0.31.20", {"start": v(-187.5, 393.75) * mm, "end": v(-172.5, 393.75) * mm, "construction": true});
            skCircle(sketch, "E6.0.31.21", {"center": v(-52.5, 393.75) * mm, "radius": 2.5 * mm});
            skCircle(sketch, "E6.0.31.22", {"center": v(187.5, 393.75) * mm, "radius": 2.5 * mm});
            skCircle(sketch, "E6.0.31.23", {"center": v(-97.5, 393.75) * mm, "radius": 2.5 * mm});
            skCircle(sketch, "E6.0.31.24", {"center": v(142.5, 393.75) * mm, "radius": 2.5 * mm});
            skCircle(sketch, "E6.0.31.25", {"center": v(-67.5, 393.75) * mm, "radius": 2.5 * mm});
            skCircle(sketch, "E6.0.31.26", {"center": v(172.5, 393.75) * mm, "radius": 2.5 * mm});
            skLineSegment(sketch, "E6.direction1", {"start": v(-187.5, -381.25) * mm, "end": v(-162.5, -381.25) * mm, "construction": true});
            skLineSegment(sketch, "E6.direction2", {"start": v(-187.5, -381.25) * mm, "end": v(-187.5, -356.25) * mm, "construction": true});
            skSolve(sketch);
        }
        {
            var Q0;
            Q0=makeQuery(id+"F0.imprint","IMPRINT",FACE,{"disambiguationData":[TD([[makeQuery(id+"F0.imprint","IMPRINT",EDGE,{"derivedFrom":sQuery(id+"F0.wireOp",EDGE,"E0.bottom")}),1.0]])]});
            extrude(context, id + "F1", {"entities" : qUnion([Q0]), "depth" : 1 * mm, "offsetDistance" : 25 * mm});
        }
    });
